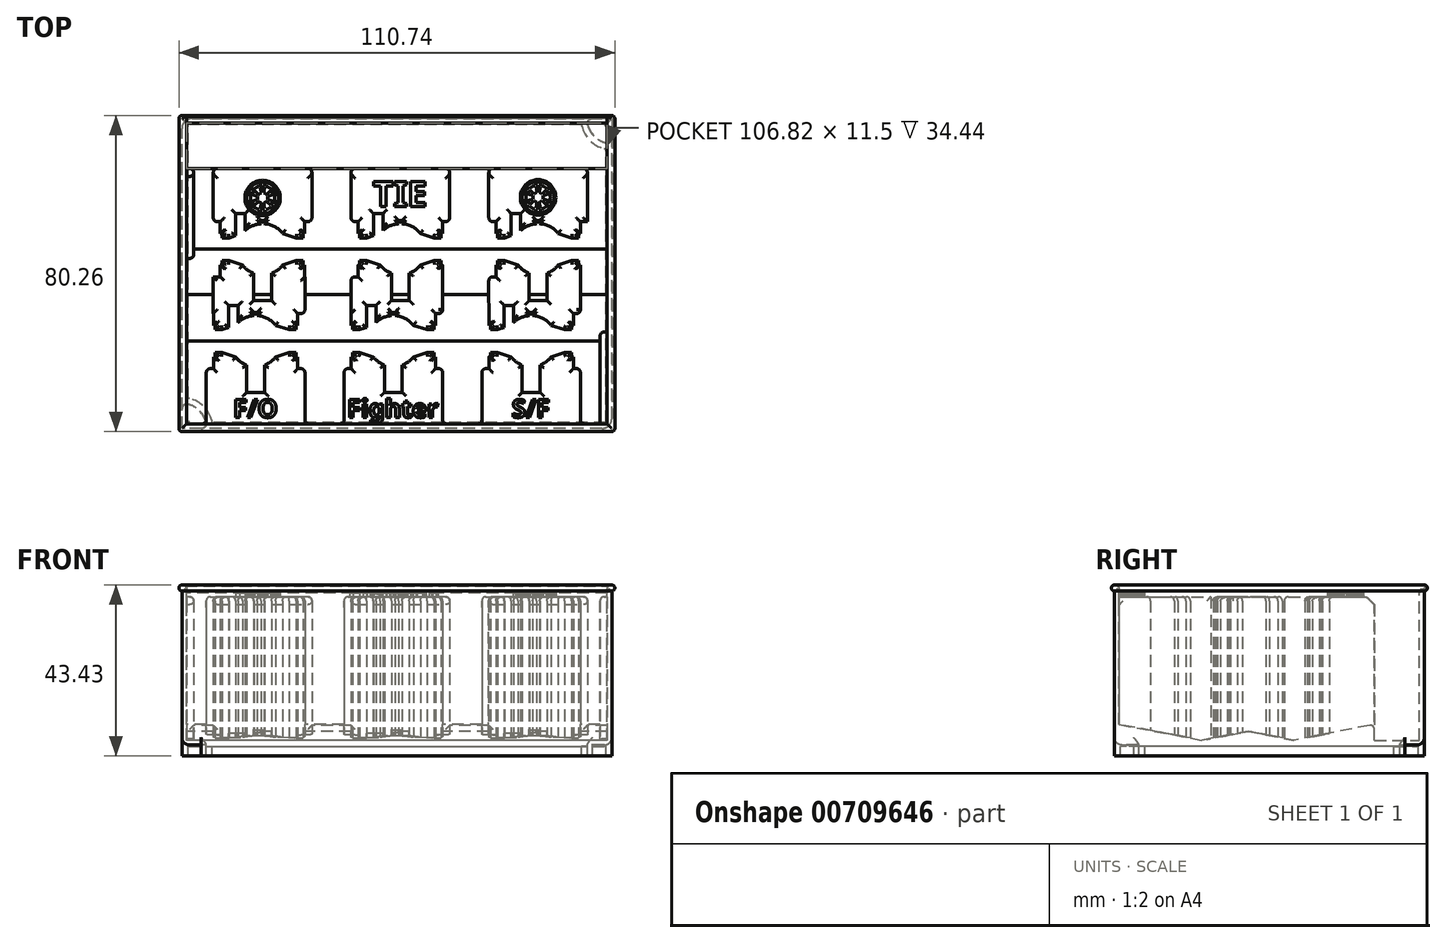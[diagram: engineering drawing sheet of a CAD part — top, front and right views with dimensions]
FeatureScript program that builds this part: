
annotation { "Feature Type Name" : "Feature", "Feature Type Description" : "" }
export const myFeature = defineFeature(function(context is Context, id is Id, definition is map)
    precondition{}
    {
        {
            var Q0;
            Q0=qCreatedBy(makeId("Front.planeOp"),FACE);
            var sketch = newSketch(context, id + "F0", { "sketchPlane" : qUnion([Q0])});
            skLineSegment(sketch, "E0.bottom", {"start": v(54.61, -20.32) * mm, "end": v(-54.61, -20.32) * mm});
            skLineSegment(sketch, "E0.top", {"start": v(54.61, 20.32) * mm, "end": v(-54.61, 20.32) * mm});
            skLineSegment(sketch, "E0.left", {"start": v(54.61, -20.32) * mm, "end": v(54.61, 20.32) * mm});
            skLineSegment(sketch, "E0.right", {"start": v(-54.61, -20.32) * mm, "end": v(-54.61, 20.32) * mm});
            skPoint(sketch, "E0.middle", {"position": v(0, 0) * mm});
            skSolve(sketch);
        }
        {
            var Q0;
            Q0=makeQuery(id+"F0.imprint","IMPRINT",FACE,{"disambiguationData":[TD([[makeQuery(id+"F0.imprint","IMPRINT",EDGE,{"derivedFrom":sQuery(id+"F0.wireOp",EDGE,"E0.bottom")}),-1.0]])]});
            extrude(context, id + "F1", {"entities" : qUnion([Q0]), "depth" : 78.74 * mm, "symmetric" : true});
        }
        {
            var Q0;
            Q0=makeQuery(id+"F1.opExtrude","SWEPT_FACE",FACE,{"disambiguationData":[OSD([sQuery(id+"F0.wireOp",EDGE,"E0.top")])]});
            shell(context, id + "F2", {"entities" : qUnion([Q0]), "thickness" : 1.2 * mm});
        }
        {
            var Q0;
            Q0=makeQuery(id+"F1.opExtrude","CAP_FACE",FACE,{"disambiguationData":[OSD([sQuery(id+"F0.wireOp",EDGE,"E0.bottom"),sQuery(id+"F0.wireOp",EDGE,"E0.top"),sQuery(id+"F0.wireOp",EDGE,"E0.left"),sQuery(id+"F0.wireOp",EDGE,"E0.right")])],"isStart":false});
            var sketch = newSketch(context, id + "F3", { "sketchPlane" : qUnion([Q0])});
            skArc(sketch, "E1", {"start": v(-54.61, 20.32) * mm, "mid": v(-55.37, 19.56) * mm, "end": v(-54.61, 18.8) * mm});
            skSolve(sketch);
        }
        {
            var Q0;
            {var subQ0=sQuery(id+"F3.wireOp",EDGE,"E1");Q0=makeQuery(id+"F3.imprint","IMPRINT",FACE,{"disambiguationData":[TD([[makeQuery(id+"F3.imprint","IMPRINT",EDGE,{"derivedFrom":subQ0}),1.0]])]});}
            var Q1;
            Q1=makeQuery(id+"F1.opExtrude","SWEPT_EDGE",EDGE,{"disambiguationData":[OSD([sQuery(id+"F0.wireOp",EDGE,"E0.top"),sQuery(id+"F0.wireOp",EDGE,"E0.right")])]});
            var Q2;
            Q2=makeQuery(id+"F1.opExtrude","CAP_EDGE",EDGE,{"disambiguationData":[OSD([sQuery(id+"F0.wireOp",EDGE,"E0.top")])],"isStart":true});
            var Q3;
            Q3=makeQuery(id+"F1.opExtrude","SWEPT_EDGE",EDGE,{"disambiguationData":[OSD([sQuery(id+"F0.wireOp",EDGE,"E0.top"),sQuery(id+"F0.wireOp",EDGE,"E0.left")])]});
            var Q4;
            Q4=makeQuery(id+"F1.opExtrude","CAP_EDGE",EDGE,{"disambiguationData":[OSD([sQuery(id+"F0.wireOp",EDGE,"E0.top")])],"isStart":false});
            sweep(context, id + "F4", {"operationType" : NewBodyOperationType.ADD, "profiles" : qUnion([Q0]), "path" : qUnion([Q1, Q2, Q3, Q4])});
        }
        {
            var Q0;
            Q0=makeQuery(id+"F1.opExtrude","SWEPT_FACE",FACE,{"disambiguationData":[OSD([sQuery(id+"F0.wireOp",EDGE,"E0.bottom")])]});
            var sketch = newSketch(context, id + "F5", { "sketchPlane" : qUnion([Q0])});
            skLineSegment(sketch, "E2.bottom", {"start": v(54.61, 39.37) * mm, "end": v(49.7, 39.37) * mm});
            skLineSegment(sketch, "E2.left", {"start": v(54.61, 39.37) * mm, "end": v(54.61, 34.45) * mm});
            skPoint(sketch, "E3.newPointA", {"position": v(48.26, 19.05) * mm});
            skArc(sketch, "E4", {"start": v(48.46, 37.78) * mm, "mid": v(50.12, 34.88) * mm, "end": v(53.02, 33.22) * mm});
            skPoint(sketch, "E5.visualSharp", {"position": v(48.26, 39.37) * mm});
            skArc(sketch, "E5.filletArc", {"start": v(49.7, 39.37) * mm, "mid": v(48.69, 38.88) * mm, "end": v(48.46, 37.78) * mm});
            skPoint(sketch, "E6.visualSharp", {"position": v(54.61, 33.02) * mm});
            skArc(sketch, "E6.filletArc", {"start": v(53.02, 33.22) * mm, "mid": v(54.12, 33.45) * mm, "end": v(54.6, 34.45) * mm});
            skArc(sketch, "E7.MirrorCS", {"start": v(-49.7, 39.37) * mm, "mid": v(-48.69, 38.88) * mm, "end": v(-48.46, 37.78) * mm});
            skArc(sketch, "E8.MirrorCS", {"start": v(-48.46, 37.78) * mm, "mid": v(-50.12, 34.88) * mm, "end": v(-53.02, 33.22) * mm});
            skArc(sketch, "E9.MirrorCS", {"start": v(-53.02, 33.22) * mm, "mid": v(-54.12, 33.45) * mm, "end": v(-54.6, 34.45) * mm});
            skLineSegment(sketch, "E10.MirrorCS", {"start": v(-54.61, 39.37) * mm, "end": v(-54.61, 34.45) * mm});
            skLineSegment(sketch, "E11.MirrorCS", {"start": v(-54.61, 39.37) * mm, "end": v(-49.7, 39.37) * mm});
            skArc(sketch, "E12.MirrorCS", {"start": v(-48.46, -37.78) * mm, "mid": v(-50.12, -34.88) * mm, "end": v(-53.02, -33.22) * mm});
            skArc(sketch, "E13.MirrorCS", {"start": v(-49.7, -39.37) * mm, "mid": v(-48.69, -38.88) * mm, "end": v(-48.46, -37.78) * mm});
            skLineSegment(sketch, "E14.MirrorCS", {"start": v(-54.6, -39.37) * mm, "end": v(-49.7, -39.37) * mm});
            skLineSegment(sketch, "E15.MirrorCS", {"start": v(-54.6, -39.37) * mm, "end": v(-54.6, -34.45) * mm});
            skArc(sketch, "E16.MirrorCS", {"start": v(-53.02, -33.22) * mm, "mid": v(-54.12, -33.45) * mm, "end": v(-54.6, -34.45) * mm});
            skArc(sketch, "E17.MirrorCS", {"start": v(49.7, -39.37) * mm, "mid": v(48.69, -38.88) * mm, "end": v(48.46, -37.78) * mm});
            skArc(sketch, "E18.MirrorCS", {"start": v(48.46, -37.78) * mm, "mid": v(50.12, -34.88) * mm, "end": v(53.02, -33.22) * mm});
            skArc(sketch, "E19.MirrorCS", {"start": v(53.02, -33.22) * mm, "mid": v(54.12, -33.45) * mm, "end": v(54.6, -34.45) * mm});
            skLineSegment(sketch, "E20.MirrorCS", {"start": v(54.6, -39.37) * mm, "end": v(54.6, -34.45) * mm});
            skLineSegment(sketch, "E21.MirrorCS", {"start": v(54.6, -39.37) * mm, "end": v(49.7, -39.37) * mm});
            skSolve(sketch);
        }
        {
            var Q0;
            Q0=makeQuery(id+"F5.imprint","IMPRINT",FACE,{"disambiguationData":[TD([[makeQuery(id+"F5.imprint","IMPRINT",EDGE,{"derivedFrom":sQuery(id+"F5.wireOp",EDGE,"E2.bottom")}),1.0]])]});
            var Q1;
            Q1=makeQuery(id+"F5.imprint","IMPRINT",FACE,{"disambiguationData":[TD([[makeQuery(id+"F5.imprint","IMPRINT",EDGE,{"derivedFrom":sQuery(id+"F5.wireOp",EDGE,"E8.MirrorCS")}),-1.0]])]});
            var Q2;
            Q2=makeQuery(id+"F5.imprint","IMPRINT",FACE,{"disambiguationData":[TD([[makeQuery(id+"F5.imprint","IMPRINT",EDGE,{"derivedFrom":sQuery(id+"F5.wireOp",EDGE,"E12.MirrorCS")}),1.0]])]});
            var Q3;
            Q3=makeQuery(id+"F5.imprint","IMPRINT",FACE,{"disambiguationData":[TD([[makeQuery(id+"F5.imprint","IMPRINT",EDGE,{"derivedFrom":sQuery(id+"F5.wireOp",EDGE,"E17.MirrorCS")}),-1.0]])]});
            extrude(context, id + "F6", {"entities" : qUnion([Q0, Q1, Q2, Q3]), "operationType" : NewBodyOperationType.ADD, "depth" : 2.8 * mm});
        }
        {
            var Q0;
            Q0=makeQuery(id+"F6.opExtrude","CAP_FACE",FACE,{"disambiguationData":[OSD([sQuery(id+"F5.wireOp",EDGE,"E2.bottom"),sQuery(id+"F5.wireOp",EDGE,"E2.left"),sQuery(id+"F5.wireOp",EDGE,"E4"),sQuery(id+"F5.wireOp",EDGE,"E5.filletArc"),sQuery(id+"F5.wireOp",EDGE,"E6.filletArc")])],"isStart":false});
            var Q1;
            Q1=makeQuery(id+"F6.opExtrude","CAP_FACE",FACE,{"disambiguationData":[OSD([sQuery(id+"F5.wireOp",EDGE,"E8.MirrorCS"),sQuery(id+"F5.wireOp",EDGE,"E9.MirrorCS"),sQuery(id+"F5.wireOp",EDGE,"E10.MirrorCS"),sQuery(id+"F5.wireOp",EDGE,"E7.MirrorCS"),sQuery(id+"F5.wireOp",EDGE,"E11.MirrorCS")])],"isStart":false});
            var Q2;
            Q2=makeQuery(id+"F6.opExtrude","CAP_FACE",FACE,{"disambiguationData":[OSD([sQuery(id+"F5.wireOp",EDGE,"E12.MirrorCS"),sQuery(id+"F5.wireOp",EDGE,"E13.MirrorCS"),sQuery(id+"F5.wireOp",EDGE,"E14.MirrorCS"),sQuery(id+"F5.wireOp",EDGE,"E15.MirrorCS"),sQuery(id+"F5.wireOp",EDGE,"E16.MirrorCS")])],"isStart":false});
            var Q3;
            Q3=makeQuery(id+"F6.opExtrude","CAP_FACE",FACE,{"disambiguationData":[OSD([sQuery(id+"F5.wireOp",EDGE,"E17.MirrorCS"),sQuery(id+"F5.wireOp",EDGE,"E18.MirrorCS"),sQuery(id+"F5.wireOp",EDGE,"E19.MirrorCS"),sQuery(id+"F5.wireOp",EDGE,"E20.MirrorCS"),sQuery(id+"F5.wireOp",EDGE,"E21.MirrorCS")])],"isStart":false});
            shell(context, id + "F7", {"entities" : qUnion([Q0, Q1, Q2, Q3]), "thickness" : 1.52 * mm});
        }
        {
            var Q0;
            Q0=makeQuery(id+"F1.opExtrude","SWEPT_EDGE",EDGE,{"disambiguationData":[OSD([sQuery(id+"F0.wireOp",EDGE,"E0.bottom"),sQuery(id+"F0.wireOp",EDGE,"E0.right")])]});
            var Q1;
            Q1=makeQuery(id+"F1.opExtrude","CAP_EDGE",EDGE,{"disambiguationData":[OSD([sQuery(id+"F0.wireOp",EDGE,"E0.bottom")])],"isStart":false});
            var Q2;
            Q2=makeQuery(id+"F1.opExtrude","SWEPT_EDGE",EDGE,{"disambiguationData":[OSD([sQuery(id+"F0.wireOp",EDGE,"E0.bottom"),sQuery(id+"F0.wireOp",EDGE,"E0.left")])]});
            var Q3;
            Q3=makeQuery(id+"F1.opExtrude","CAP_EDGE",EDGE,{"disambiguationData":[OSD([sQuery(id+"F0.wireOp",EDGE,"E0.bottom")])],"isStart":true});
            fillet(context, id + "F8", {"entities" : qUnion([Q0, Q1, Q2, Q3]), "radius" : 1.9 * mm, "tangentPropagation" : true, "allowEdgeOverflow" : false});
        }
        {
            var Q0;
            Q0=makeQuery(id+"F4.opSweep","MID_CAP_EDGE",EDGE,{"disambiguationData":[OSD([sQuery(id+"F0.wireOp",EDGE,"E0.top"),sQuery(id+"F0.wireOp",EDGE,"E0.left"),sQuery(id+"F3.wireOp",EDGE,"E1")])],"capPos":3.0});
            var Q1;
            Q1=makeQuery(id+"F4.opSweep","MID_CAP_EDGE",EDGE,{"disambiguationData":[OSD([sQuery(id+"F0.wireOp",EDGE,"E0.top"),sQuery(id+"F0.wireOp",EDGE,"E0.left"),sQuery(id+"F3.wireOp",EDGE,"E1")])],"capPos":2.0});
            var Q2;
            Q2=makeQuery(id+"F4.opSweep","MID_CAP_EDGE",EDGE,{"disambiguationData":[OSD([sQuery(id+"F0.wireOp",EDGE,"E0.top"),sQuery(id+"F0.wireOp",EDGE,"E0.right"),sQuery(id+"F3.wireOp",EDGE,"E1")])],"capPos":1.0});
            var Q3;
            Q3=makeQuery(id+"F4.opSweep","CAP_EDGE",EDGE,{"disambiguationData":[OSD([sQuery(id+"F0.wireOp",EDGE,"E0.top"),sQuery(id+"F0.wireOp",EDGE,"E0.right"),sQuery(id+"F3.wireOp",EDGE,"E1")])],"isStart":true});
            fillet(context, id + "F9", {"entities" : qUnion([Q0, Q1, Q2, Q3]), "radius" : 0.76 * mm, "tangentPropagation" : true, "allowEdgeOverflow" : false});
        }
        {
            var Q0;
            Q0=makeQuery(id+"F6.boolean.opBoolean","MERGE",EDGE,{"derivedFrom":[makeQuery(id+"F1.opExtrude","CAP_EDGE",EDGE,{"disambiguationData":[OSD([sQuery(id+"F0.wireOp",EDGE,"E0.left")])],"isStart":false}),makeQuery(id+"F6.opExtrude","SWEPT_EDGE",EDGE,{"disambiguationData":[OSD([sQuery(id+"F5.wireOp",EDGE,"E2.bottom"),sQuery(id+"F5.wireOp",EDGE,"E2.left")])]})]});
            var Q1;
            Q1=makeQuery(id+"F6.boolean.opBoolean","MERGE",EDGE,{"derivedFrom":[makeQuery(id+"F1.opExtrude","CAP_EDGE",EDGE,{"disambiguationData":[OSD([sQuery(id+"F0.wireOp",EDGE,"E0.left")])],"isStart":true}),makeQuery(id+"F6.opExtrude","SWEPT_EDGE",EDGE,{"disambiguationData":[OSD([sQuery(id+"F5.wireOp",EDGE,"E20.MirrorCS"),sQuery(id+"F5.wireOp",EDGE,"E21.MirrorCS")])]})]});
            var Q2;
            Q2=makeQuery(id+"F6.boolean.opBoolean","MERGE",EDGE,{"derivedFrom":[makeQuery(id+"F1.opExtrude","CAP_EDGE",EDGE,{"disambiguationData":[OSD([sQuery(id+"F0.wireOp",EDGE,"E0.right")])],"isStart":false}),makeQuery(id+"F6.opExtrude","SWEPT_EDGE",EDGE,{"disambiguationData":[OSD([sQuery(id+"F5.wireOp",EDGE,"E10.MirrorCS"),sQuery(id+"F5.wireOp",EDGE,"E11.MirrorCS")])]})]});
            var Q3;
            Q3=makeQuery(id+"F6.boolean.opBoolean","MERGE",EDGE,{"derivedFrom":[makeQuery(id+"F1.opExtrude","CAP_EDGE",EDGE,{"disambiguationData":[OSD([sQuery(id+"F0.wireOp",EDGE,"E0.right")])],"isStart":true}),makeQuery(id+"F6.opExtrude","SWEPT_EDGE",EDGE,{"disambiguationData":[OSD([sQuery(id+"F5.wireOp",EDGE,"E14.MirrorCS"),sQuery(id+"F5.wireOp",EDGE,"E15.MirrorCS")])]})]});
            fillet(context, id + "F10", {"entities" : qUnion([Q0, Q1, Q2, Q3]), "radius" : 2.54 * mm, "tangentPropagation" : true, "allowEdgeOverflow" : false});
        }
        {
            var Q0;
            Q0=makeQuery(id+"F2.opShell","OFFSET_FACE",FACE,{"disambiguationData":[OSD([sQuery(id+"F0.wireOp",EDGE,"E0.bottom")])]});
            var sketch = newSketch(context, id + "F11", { "sketchPlane" : qUnion([Q0])});
            skPoint(sketch, "E22.0", {"position": v(-53.4, -38.17) * mm});
            skArc(sketch, "E23", {"start": v(-41, -21.17) * mm, "mid": v(-39.72, -22.42) * mm, "end": v(-38.14, -23.27) * mm});
            skLineSegment(sketch, "E24.bottom", {"start": v(-23.36, -0.83) * mm, "end": v(-23.36, -10.17) * mm});
            skLineSegment(sketch, "E25.left", {"start": v(-27.36, -14.27) * mm, "end": v(-25.56, -14.27) * mm});
            skLineSegment(sketch, "E26", {"start": v(-30.76, -13.17) * mm, "end": v(-27.36, -14.27) * mm});
            skLineSegment(sketch, "E27.MirrorCS", {"start": v(-30.76, -21.17) * mm, "end": v(-27.36, -20.07) * mm});
            skLineSegment(sketch, "E28.MirrorCS", {"start": v(-27.36, -20.07) * mm, "end": v(-25.56, -20.07) * mm});
            skLineSegment(sketch, "E29.MirrorCS", {"start": v(-23.34, -38.17) * mm, "end": v(-18.34, -38.17) * mm});
            skLineSegment(sketch, "E30.MirrorCS", {"start": v(-44.4, -20.07) * mm, "end": v(-46.2, -20.07) * mm});
            skLineSegment(sketch, "E31.MirrorCS", {"start": v(-48.4, -38.17) * mm, "end": v(-53.4, -38.17) * mm});
            skLineSegment(sketch, "E32.MirrorCS", {"start": v(-42.7, -13.72) * mm, "end": v(-44.4, -14.27) * mm});
            skLineSegment(sketch, "E33.MirrorCS", {"start": v(-41, -21.17) * mm, "end": v(-44.4, -20.07) * mm});
            skLineSegment(sketch, "E34.MirrorCS", {"start": v(-53.4, 3.83) * mm, "end": v(-53.4, -17.17) * mm});
            skLineSegment(sketch, "E35.MirrorCS", {"start": v(-51.64, 3.83) * mm, "end": v(-53.4, 3.83) * mm});
            skArc(sketch, "E36.MirrorC", {"start": v(-40.3, -12.4) * mm, "mid": v(-38.45, -11.2) * mm, "end": v(-36.29, -10.68) * mm});
            skLineSegment(sketch, "E37.MirrorCS", {"start": v(-53.4, -38.17) * mm, "end": v(-53.4, -17.17) * mm});
            skLineSegment(sketch, "E38", {"start": v(-42.7, -13.72) * mm, "end": v(-42.7, -8.1) * mm});
            skLineSegment(sketch, "E39", {"start": v(-40.3, -12.4) * mm, "end": v(-40.3, -8.1) * mm});
            skLineSegment(sketch, "E40", {"start": v(-40.3, -8.1) * mm, "end": v(-42.7, -8.1) * mm});
            skArc(sketch, "E41.trimOffspring", {"start": v(-30.76, -13.17) * mm, "mid": v(-32.86, -11.42) * mm, "end": v(-35.49, -10.68) * mm});
            skArc(sketch, "E42.trimOffspring", {"start": v(-30.76, -21.17) * mm, "mid": v(-32.05, -22.42) * mm, "end": v(-33.64, -23.27) * mm});
            skLineSegment(sketch, "E43", {"start": v(-25.16, -13.17) * mm, "end": v(-25.56, -13.17) * mm});
            skLineSegment(sketch, "E44", {"start": v(-25.56, -13.17) * mm, "end": v(-25.56, -14.27) * mm});
            skLineSegment(sketch, "E45.MirrorCS", {"start": v(-25.56, -21.17) * mm, "end": v(-25.56, -20.07) * mm});
            skLineSegment(sketch, "E46.MirrorCS", {"start": v(-46.2, -13.17) * mm, "end": v(-46.2, -14.27) * mm});
            skLineSegment(sketch, "E47.MirrorCS", {"start": v(-46.2, -21.17) * mm, "end": v(-46.2, -20.07) * mm});
            skLineSegment(sketch, "E48", {"start": v(-46.2, -14.27) * mm, "end": v(-44.4, -14.27) * mm});
            skLineSegment(sketch, "E49", {"start": v(-38.14, -30.17) * mm, "end": v(-33.64, -30.17) * mm});
            skLineSegment(sketch, "E50", {"start": v(-38.14, -30.17) * mm, "end": v(-38.14, -23.27) * mm});
            skLineSegment(sketch, "E51", {"start": v(-33.64, -30.17) * mm, "end": v(-33.64, -23.27) * mm});
            skArc(sketch, "E52.trimOffspring", {"start": v(-38.14, -23.27) * mm, "mid": v(-39.72, -22.42) * mm, "end": v(-41, -21.17) * mm});
            skLineSegment(sketch, "E53", {"start": v(-35.89, -9.87) * mm, "end": v(-35.49, -9.87) * mm});
            skLineSegment(sketch, "E54", {"start": v(-35.49, -9.87) * mm, "end": v(-35.49, -10.68) * mm});
            skLineSegment(sketch, "E55", {"start": v(-35.89, -9.87) * mm, "end": v(-36.29, -9.87) * mm});
            skLineSegment(sketch, "E56", {"start": v(-36.29, -9.87) * mm, "end": v(-36.29, -10.68) * mm});
            skArc(sketch, "E57.trimOffspring", {"start": v(-35.49, -10.68) * mm, "mid": v(-32.86, -11.42) * mm, "end": v(-30.76, -13.17) * mm});
            skArc(sketch, "E58.trimOffspring", {"start": v(-36.29, -10.68) * mm, "mid": v(-38.45, -11.2) * mm, "end": v(-40.3, -12.4) * mm});
            skLineSegment(sketch, "E59.MirrorCS", {"start": v(-25.16, -21.17) * mm, "end": v(-25.56, -21.17) * mm});
            skLineSegment(sketch, "E60.MirrorCS", {"start": v(-46.6, -21.17) * mm, "end": v(-46.2, -21.17) * mm});
            skLineSegment(sketch, "E61.MirrorCS", {"start": v(-46.6, -13.17) * mm, "end": v(-46.2, -13.17) * mm});
            skLineSegment(sketch, "E62", {"start": v(-23.36, -10.17) * mm, "end": v(-25.16, -10.17) * mm});
            skLineSegment(sketch, "E63", {"start": v(-25.16, -10.17) * mm, "end": v(-25.16, -13.17) * mm});
            skLineSegment(sketch, "E64.MirrorCS", {"start": v(-23.36, -38.17) * mm, "end": v(-23.36, -24.17) * mm});
            skLineSegment(sketch, "E65.MirrorCS", {"start": v(-25.16, -24.17) * mm, "end": v(-25.16, -21.17) * mm});
            skLineSegment(sketch, "E66.MirrorCS", {"start": v(-23.36, -24.17) * mm, "end": v(-25.16, -24.17) * mm});
            skLineSegment(sketch, "E67.MirrorCS", {"start": v(-48.4, -38.17) * mm, "end": v(-48.4, -24.17) * mm});
            skLineSegment(sketch, "E68.MirrorCS", {"start": v(-48.41, -24.17) * mm, "end": v(-46.61, -24.17) * mm});
            skLineSegment(sketch, "E69.MirrorCS", {"start": v(-46.6, -24.17) * mm, "end": v(-46.6, -21.17) * mm});
            skLineSegment(sketch, "E70.MirrorCS", {"start": v(-46.6, -10.17) * mm, "end": v(-46.6, -13.17) * mm});
            skLineSegment(sketch, "E71.MirrorCS", {"start": v(-46.64, -10.17) * mm, "end": v(-46.61, -10.17) * mm});
            skLineSegment(sketch, "E72", {"start": v(-18.34, -38.17) * mm, "end": v(-17.54, -38.17) * mm, "construction": true});
            skPoint(sketch, "E73.1.0.0", {"position": v(-18.4, -38.17) * mm});
            skLineSegment(sketch, "E73.1.0.1", {"start": v(-6, -21.17) * mm, "end": v(-9.4, -20.07) * mm});
            skLineSegment(sketch, "E73.1.0.2", {"start": v(-5.3, -12.4) * mm, "end": v(-5.3, -8.1) * mm});
            skLineSegment(sketch, "E73.1.0.3", {"start": v(4.24, -13.17) * mm, "end": v(7.64, -14.27) * mm});
            skPoint(sketch, "E73.1.0.5", {"position": v(-0.89, -17.17) * mm});
            skLineSegment(sketch, "E73.1.0.10", {"start": v(11.66, -38.17) * mm, "end": v(16.66, -38.17) * mm});
            skLineSegment(sketch, "E73.1.0.11", {"start": v(1.36, -30.17) * mm, "end": v(1.36, -23.27) * mm});
            skLineSegment(sketch, "E73.1.0.12", {"start": v(11.64, -38.17) * mm, "end": v(11.64, -24.17) * mm});
            skArc(sketch, "E73.1.0.13", {"start": v(4.24, -13.17) * mm, "mid": v(2.14, -11.42) * mm, "end": v(-0.49, -10.68) * mm});
            skLineSegment(sketch, "E73.1.0.14", {"start": v(-11.61, -10.17) * mm, "end": v(-11.61, -13.17) * mm});
            skLineSegment(sketch, "E73.1.0.15", {"start": v(-3.14, -30.17) * mm, "end": v(1.36, -30.17) * mm});
            skLineSegment(sketch, "E73.1.0.16", {"start": v(-3.14, -30.17) * mm, "end": v(-3.14, -23.27) * mm});
            skLineSegment(sketch, "E73.1.0.18", {"start": v(-13.4, -38.17) * mm, "end": v(-18.4, -38.17) * mm});
            skLineSegment(sketch, "E73.1.0.19", {"start": v(-7.7, -13.72) * mm, "end": v(-7.7, -8.1) * mm});
            skArc(sketch, "E73.1.0.20", {"start": v(-0.49, -10.68) * mm, "mid": v(2.14, -11.42) * mm, "end": v(4.24, -13.17) * mm});
            skArc(sketch, "E73.1.0.23", {"start": v(-1.29, -10.68) * mm, "mid": v(-3.45, -11.2) * mm, "end": v(-5.3, -12.4) * mm});
            skLineSegment(sketch, "E73.1.0.24", {"start": v(4.24, -21.17) * mm, "end": v(7.64, -20.07) * mm});
            skLineSegment(sketch, "E73.1.0.25", {"start": v(-13.4, -38.17) * mm, "end": v(-13.4, -24.17) * mm});
            skLineSegment(sketch, "E73.1.0.26", {"start": v(9.84, -10.17) * mm, "end": v(9.84, -13.17) * mm});
            skArc(sketch, "E73.1.0.27", {"start": v(-5.3, -12.4) * mm, "mid": v(-3.45, -11.2) * mm, "end": v(-1.29, -10.68) * mm});
            skLineSegment(sketch, "E73.1.0.28", {"start": v(-13.4, -38.17) * mm, "end": v(-18.4, -38.17) * mm});
            skLineSegment(sketch, "E73.1.0.29", {"start": v(-7.7, -13.72) * mm, "end": v(-9.4, -14.27) * mm});
            skLineSegment(sketch, "E73.1.0.30", {"start": v(-11.64, -10.17) * mm, "end": v(-11.61, -10.17) * mm});
            skLineSegment(sketch, "E73.1.0.31", {"start": v(9.84, -21.17) * mm, "end": v(9.44, -21.17) * mm});
            skLineSegment(sketch, "E73.1.0.32", {"start": v(7.64, -20.07) * mm, "end": v(9.44, -20.07) * mm});
            skLineSegment(sketch, "E73.1.0.33", {"start": v(9.44, -21.17) * mm, "end": v(9.44, -20.07) * mm});
            skLineSegment(sketch, "E73.1.0.34", {"start": v(-11.6, -13.17) * mm, "end": v(-11.2, -13.17) * mm});
            skLineSegment(sketch, "E73.1.0.35", {"start": v(11.64, -24.17) * mm, "end": v(9.84, -24.17) * mm});
            skLineSegment(sketch, "E73.1.0.36", {"start": v(-11.2, -14.27) * mm, "end": v(-9.4, -14.27) * mm});
            skLineSegment(sketch, "E73.1.0.37", {"start": v(7.64, -14.27) * mm, "end": v(9.44, -14.27) * mm});
            skLineSegment(sketch, "E73.1.0.38", {"start": v(9.84, -24.17) * mm, "end": v(9.84, -21.17) * mm});
            skLineSegment(sketch, "E73.1.0.39", {"start": v(-13.4, -24.17) * mm, "end": v(-11.61, -24.17) * mm});
            skLineSegment(sketch, "E73.1.0.40", {"start": v(-11.6, -21.17) * mm, "end": v(-11.2, -21.17) * mm});
            skLineSegment(sketch, "E73.1.0.41", {"start": v(-9.4, -20.07) * mm, "end": v(-11.2, -20.07) * mm});
            skLineSegment(sketch, "E73.1.0.42", {"start": v(9.84, -13.17) * mm, "end": v(9.44, -13.17) * mm});
            skLineSegment(sketch, "E73.1.0.43", {"start": v(-11.61, -24.17) * mm, "end": v(-11.61, -21.17) * mm});
            skLineSegment(sketch, "E73.1.0.44", {"start": v(-5.3, -8.1) * mm, "end": v(-7.7, -8.1) * mm});
            skLineSegment(sketch, "E73.1.0.45", {"start": v(-11.2, -21.17) * mm, "end": v(-11.2, -20.07) * mm});
            skLineSegment(sketch, "E73.1.0.46", {"start": v(-11.2, -13.17) * mm, "end": v(-11.2, -14.27) * mm});
            skLineSegment(sketch, "E73.1.0.47", {"start": v(11.64, -10.17) * mm, "end": v(9.84, -10.17) * mm});
            skArc(sketch, "E73.1.0.48", {"start": v(4.24, -21.17) * mm, "mid": v(2.95, -22.42) * mm, "end": v(1.36, -23.27) * mm});
            skLineSegment(sketch, "E73.1.0.49", {"start": v(9.44, -13.17) * mm, "end": v(9.44, -14.27) * mm});
            skArc(sketch, "E73.1.0.50", {"start": v(-6, -21.17) * mm, "mid": v(-4.72, -22.42) * mm, "end": v(-3.14, -23.27) * mm});
            skLineSegment(sketch, "E73.1.0.51", {"start": v(16.66, -38.17) * mm, "end": v(17.46, -38.17) * mm, "construction": true});
            skArc(sketch, "E73.1.0.52", {"start": v(-3.14, -23.27) * mm, "mid": v(-4.72, -22.42) * mm, "end": v(-6, -21.17) * mm});
            skLineSegment(sketch, "E73.1.0.53", {"start": v(-0.89, -9.87) * mm, "end": v(-1.29, -9.87) * mm});
            skLineSegment(sketch, "E73.1.0.54", {"start": v(-0.49, -9.87) * mm, "end": v(-0.49, -10.68) * mm});
            skLineSegment(sketch, "E73.1.0.55", {"start": v(-1.29, -9.87) * mm, "end": v(-1.29, -10.68) * mm});
            skLineSegment(sketch, "E73.1.0.56", {"start": v(-0.89, -9.87) * mm, "end": v(-0.49, -9.87) * mm});
            skPoint(sketch, "E73.2.0.0", {"position": v(16.6, -38.17) * mm});
            skLineSegment(sketch, "E73.2.0.1", {"start": v(29, -21.17) * mm, "end": v(25.6, -20.07) * mm});
            skLineSegment(sketch, "E73.2.0.2", {"start": v(29.7, -12.4) * mm, "end": v(29.7, -8.1) * mm});
            skLineSegment(sketch, "E73.2.0.3", {"start": v(39.24, -13.17) * mm, "end": v(42.64, -14.27) * mm});
            skPoint(sketch, "E73.2.0.5", {"position": v(34.11, -17.17) * mm});
            skLineSegment(sketch, "E73.2.0.10", {"start": v(46.66, -38.17) * mm, "end": v(51.66, -38.17) * mm});
            skLineSegment(sketch, "E73.2.0.11", {"start": v(36.36, -30.17) * mm, "end": v(36.36, -23.27) * mm});
            skLineSegment(sketch, "E73.2.0.12", {"start": v(46.64, -38.17) * mm, "end": v(46.64, -24.17) * mm});
            skArc(sketch, "E73.2.0.13", {"start": v(39.24, -13.17) * mm, "mid": v(37.14, -11.42) * mm, "end": v(34.51, -10.68) * mm});
            skLineSegment(sketch, "E73.2.0.15", {"start": v(31.86, -30.17) * mm, "end": v(36.36, -30.17) * mm});
            skLineSegment(sketch, "E73.2.0.16", {"start": v(31.86, -30.17) * mm, "end": v(31.86, -23.27) * mm});
            skLineSegment(sketch, "E73.2.0.18", {"start": v(21.6, -38.17) * mm, "end": v(16.6, -38.17) * mm});
            skLineSegment(sketch, "E73.2.0.19", {"start": v(27.3, -13.72) * mm, "end": v(27.3, -8.1) * mm});
            skArc(sketch, "E73.2.0.20", {"start": v(34.51, -10.68) * mm, "mid": v(37.14, -11.42) * mm, "end": v(39.24, -13.17) * mm});
            skArc(sketch, "E73.2.0.23", {"start": v(33.71, -10.68) * mm, "mid": v(31.55, -11.2) * mm, "end": v(29.7, -12.4) * mm});
            skLineSegment(sketch, "E73.2.0.24", {"start": v(39.24, -21.17) * mm, "end": v(42.64, -20.07) * mm});
            skLineSegment(sketch, "E73.2.0.25", {"start": v(21.6, -38.17) * mm, "end": v(21.6, -24.17) * mm});
            skLineSegment(sketch, "E73.2.0.26", {"start": v(44.84, -10.17) * mm, "end": v(44.84, -13.17) * mm});
            skArc(sketch, "E73.2.0.27", {"start": v(29.7, -12.4) * mm, "mid": v(31.55, -11.2) * mm, "end": v(33.71, -10.68) * mm});
            skLineSegment(sketch, "E73.2.0.28", {"start": v(21.6, -38.17) * mm, "end": v(16.6, -38.17) * mm});
            skLineSegment(sketch, "E73.2.0.29", {"start": v(27.3, -13.72) * mm, "end": v(25.6, -14.27) * mm});
            skLineSegment(sketch, "E73.2.0.31", {"start": v(44.84, -21.17) * mm, "end": v(44.44, -21.17) * mm});
            skLineSegment(sketch, "E73.2.0.32", {"start": v(42.64, -20.07) * mm, "end": v(44.44, -20.07) * mm});
            skLineSegment(sketch, "E73.2.0.33", {"start": v(44.44, -21.17) * mm, "end": v(44.44, -20.07) * mm});
            skLineSegment(sketch, "E73.2.0.34", {"start": v(23.4, -13.17) * mm, "end": v(23.8, -13.17) * mm});
            skLineSegment(sketch, "E73.2.0.35", {"start": v(46.64, -24.17) * mm, "end": v(44.84, -24.17) * mm});
            skLineSegment(sketch, "E73.2.0.36", {"start": v(23.8, -14.27) * mm, "end": v(25.6, -14.27) * mm});
            skLineSegment(sketch, "E73.2.0.37", {"start": v(42.64, -14.27) * mm, "end": v(44.44, -14.27) * mm});
            skLineSegment(sketch, "E73.2.0.38", {"start": v(44.84, -24.17) * mm, "end": v(44.84, -21.17) * mm});
            skLineSegment(sketch, "E73.2.0.39", {"start": v(21.6, -24.17) * mm, "end": v(23.4, -24.17) * mm});
            skLineSegment(sketch, "E73.2.0.40", {"start": v(23.4, -21.17) * mm, "end": v(23.8, -21.17) * mm});
            skLineSegment(sketch, "E73.2.0.41", {"start": v(25.6, -20.07) * mm, "end": v(23.8, -20.07) * mm});
            skLineSegment(sketch, "E73.2.0.42", {"start": v(44.84, -13.17) * mm, "end": v(44.44, -13.17) * mm});
            skLineSegment(sketch, "E73.2.0.43", {"start": v(23.4, -24.17) * mm, "end": v(23.4, -21.17) * mm});
            skLineSegment(sketch, "E73.2.0.44", {"start": v(29.7, -8.1) * mm, "end": v(27.3, -8.1) * mm});
            skLineSegment(sketch, "E73.2.0.45", {"start": v(23.8, -21.17) * mm, "end": v(23.8, -20.07) * mm});
            skLineSegment(sketch, "E73.2.0.46", {"start": v(23.8, -13.17) * mm, "end": v(23.8, -14.27) * mm});
            skLineSegment(sketch, "E73.2.0.47", {"start": v(46.64, -10.17) * mm, "end": v(44.84, -10.17) * mm});
            skArc(sketch, "E73.2.0.48", {"start": v(39.24, -21.17) * mm, "mid": v(37.95, -22.42) * mm, "end": v(36.36, -23.27) * mm});
            skLineSegment(sketch, "E73.2.0.49", {"start": v(44.44, -13.17) * mm, "end": v(44.44, -14.27) * mm});
            skArc(sketch, "E73.2.0.50", {"start": v(29, -21.17) * mm, "mid": v(30.28, -22.42) * mm, "end": v(31.86, -23.27) * mm});
            skLineSegment(sketch, "E73.2.0.51", {"start": v(51.66, -38.17) * mm, "end": v(52.46, -38.17) * mm, "construction": true});
            skArc(sketch, "E73.2.0.52", {"start": v(31.86, -23.27) * mm, "mid": v(30.28, -22.42) * mm, "end": v(29, -21.17) * mm});
            skLineSegment(sketch, "E73.2.0.53", {"start": v(34.11, -9.87) * mm, "end": v(33.71, -9.87) * mm});
            skLineSegment(sketch, "E73.2.0.54", {"start": v(34.51, -9.87) * mm, "end": v(34.51, -10.68) * mm});
            skLineSegment(sketch, "E73.2.0.55", {"start": v(33.71, -9.87) * mm, "end": v(33.71, -10.68) * mm});
            skLineSegment(sketch, "E73.2.0.56", {"start": v(34.11, -9.87) * mm, "end": v(34.51, -9.87) * mm});
            skLineSegment(sketch, "E73.direction1", {"start": v(-53.41, -38.17) * mm, "end": v(-18.4, -38.17) * mm, "construction": true});
            skPoint(sketch, "E74.0", {"position": v(-51.64, -14.83) * mm});
            skArc(sketch, "E75", {"start": v(-39.24, 2.17) * mm, "mid": v(-37.95, 0.92) * mm, "end": v(-36.36, 0.07) * mm});
            skLineSegment(sketch, "E76.bottom", {"start": v(-21.59, 27.17) * mm, "end": v(-21.59, 13.17) * mm});
            skLineSegment(sketch, "E77.left", {"start": v(-25.59, 9.07) * mm, "end": v(-23.79, 9.07) * mm});
            skLineSegment(sketch, "E78", {"start": v(-28.99, 10.17) * mm, "end": v(-25.59, 9.07) * mm});
            skLineSegment(sketch, "E79.MirrorCS", {"start": v(-28.99, 2.17) * mm, "end": v(-25.59, 3.27) * mm});
            skLineSegment(sketch, "E80.MirrorCS", {"start": v(-25.59, 3.27) * mm, "end": v(-23.79, 3.27) * mm});
            skLineSegment(sketch, "E81.MirrorCS", {"start": v(-42.64, 3.27) * mm, "end": v(-44.44, 3.27) * mm});
            skLineSegment(sketch, "E82.MirrorCS", {"start": v(-40.94, 9.62) * mm, "end": v(-42.64, 9.07) * mm});
            skLineSegment(sketch, "E83.MirrorCS", {"start": v(-39.24, 2.17) * mm, "end": v(-42.64, 3.27) * mm});
            skLineSegment(sketch, "E84.MirrorCS", {"start": v(-51.64, 27.17) * mm, "end": v(-51.64, 6.17) * mm});
            skArc(sketch, "E85.MirrorC", {"start": v(-38.54, 10.93) * mm, "mid": v(-36.67, 12.14) * mm, "end": v(-34.51, 12.66) * mm});
            skLineSegment(sketch, "E86.MirrorCS", {"start": v(-51.64, 3.83) * mm, "end": v(-51.64, 6.17) * mm});
            skLineSegment(sketch, "E87", {"start": v(-40.94, 9.62) * mm, "end": v(-40.94, 15.23) * mm});
            skLineSegment(sketch, "E88", {"start": v(-38.54, 10.93) * mm, "end": v(-38.54, 15.23) * mm});
            skLineSegment(sketch, "E89", {"start": v(-38.54, 15.23) * mm, "end": v(-40.94, 15.23) * mm});
            skArc(sketch, "E90.trimOffspring", {"start": v(-28.99, 10.17) * mm, "mid": v(-31.08, 11.92) * mm, "end": v(-33.71, 12.66) * mm});
            skArc(sketch, "E91.trimOffspring", {"start": v(-28.99, 2.17) * mm, "mid": v(-30.28, 0.92) * mm, "end": v(-31.86, 0.07) * mm});
            skLineSegment(sketch, "E92", {"start": v(-23.39, 10.17) * mm, "end": v(-23.79, 10.17) * mm});
            skLineSegment(sketch, "E93", {"start": v(-23.79, 10.17) * mm, "end": v(-23.79, 9.07) * mm});
            skLineSegment(sketch, "E94.MirrorCS", {"start": v(-23.79, 2.17) * mm, "end": v(-23.79, 3.27) * mm});
            skLineSegment(sketch, "E95.MirrorCS", {"start": v(-44.44, 10.17) * mm, "end": v(-44.44, 9.07) * mm});
            skLineSegment(sketch, "E96.MirrorCS", {"start": v(-44.44, 2.17) * mm, "end": v(-44.44, 3.27) * mm});
            skLineSegment(sketch, "E97", {"start": v(-44.44, 9.07) * mm, "end": v(-42.64, 9.07) * mm});
            skLineSegment(sketch, "E98", {"start": v(-36.36, -6.83) * mm, "end": v(-31.86, -6.83) * mm});
            skLineSegment(sketch, "E99", {"start": v(-36.36, -6.83) * mm, "end": v(-36.36, 0.07) * mm});
            skLineSegment(sketch, "E100", {"start": v(-31.86, -6.83) * mm, "end": v(-31.86, 0.07) * mm});
            skArc(sketch, "E101.trimOffspring", {"start": v(-36.36, 0.07) * mm, "mid": v(-37.95, 0.92) * mm, "end": v(-39.24, 2.17) * mm});
            skLineSegment(sketch, "E102", {"start": v(-34.11, 13.47) * mm, "end": v(-33.71, 13.47) * mm});
            skLineSegment(sketch, "E103", {"start": v(-33.71, 13.47) * mm, "end": v(-33.71, 12.66) * mm});
            skLineSegment(sketch, "E104", {"start": v(-34.11, 13.47) * mm, "end": v(-34.51, 13.47) * mm});
            skLineSegment(sketch, "E105", {"start": v(-34.51, 13.47) * mm, "end": v(-34.51, 12.66) * mm});
            skArc(sketch, "E106.trimOffspring", {"start": v(-33.71, 12.66) * mm, "mid": v(-31.08, 11.92) * mm, "end": v(-28.99, 10.17) * mm});
            skArc(sketch, "E107.trimOffspring", {"start": v(-34.51, 12.66) * mm, "mid": v(-36.67, 12.14) * mm, "end": v(-38.54, 10.93) * mm});
            skLineSegment(sketch, "E108.MirrorCS", {"start": v(-23.39, 2.17) * mm, "end": v(-23.79, 2.17) * mm});
            skLineSegment(sketch, "E109.MirrorCS", {"start": v(-44.84, 2.17) * mm, "end": v(-44.44, 2.17) * mm});
            skLineSegment(sketch, "E110.MirrorCS", {"start": v(-44.84, 10.17) * mm, "end": v(-44.44, 10.17) * mm});
            skLineSegment(sketch, "E111", {"start": v(-21.59, 13.17) * mm, "end": v(-23.39, 13.17) * mm});
            skLineSegment(sketch, "E112", {"start": v(-23.39, 13.17) * mm, "end": v(-23.39, 10.17) * mm});
            skLineSegment(sketch, "E113.MirrorCS", {"start": v(-23.39, -0.83) * mm, "end": v(-23.39, 2.17) * mm});
            skLineSegment(sketch, "E114.MirrorCS", {"start": v(-23.36, -0.83) * mm, "end": v(-23.39, -0.83) * mm});
            skLineSegment(sketch, "E115.MirrorCS", {"start": v(-46.64, -10.17) * mm, "end": v(-46.64, -0.83) * mm});
            skLineSegment(sketch, "E116.MirrorCS", {"start": v(-46.64, -0.83) * mm, "end": v(-44.84, -0.83) * mm});
            skLineSegment(sketch, "E117.MirrorCS", {"start": v(-44.84, -0.83) * mm, "end": v(-44.84, 2.17) * mm});
            skLineSegment(sketch, "E118.MirrorCS", {"start": v(-44.84, 13.17) * mm, "end": v(-44.84, 10.17) * mm});
            skLineSegment(sketch, "E119.MirrorCS", {"start": v(-46.64, 27.17) * mm, "end": v(-46.64, 13.17) * mm});
            skLineSegment(sketch, "E120.MirrorCS", {"start": v(-46.64, 13.17) * mm, "end": v(-44.84, 13.17) * mm});
            skLineSegment(sketch, "E121.1.0.1", {"start": v(-4.24, 2.17) * mm, "end": v(-7.64, 3.27) * mm});
            skLineSegment(sketch, "E121.1.0.2", {"start": v(-3.54, 10.93) * mm, "end": v(-3.54, 15.23) * mm});
            skLineSegment(sketch, "E121.1.0.3", {"start": v(6.01, 10.17) * mm, "end": v(9.4, 9.07) * mm});
            skPoint(sketch, "E121.1.0.5", {"position": v(0.89, 6.17) * mm});
            skLineSegment(sketch, "E121.1.0.8", {"start": v(13.41, 27.17) * mm, "end": v(13.41, 13.17) * mm});
            skLineSegment(sketch, "E121.1.0.11", {"start": v(3.14, -6.83) * mm, "end": v(3.14, 0.07) * mm});
            skArc(sketch, "E121.1.0.13", {"start": v(6.01, 10.17) * mm, "mid": v(3.92, 11.92) * mm, "end": v(1.29, 12.66) * mm});
            skLineSegment(sketch, "E121.1.0.14", {"start": v(-9.84, 13.17) * mm, "end": v(-9.84, 10.17) * mm});
            skLineSegment(sketch, "E121.1.0.15", {"start": v(-1.36, -6.83) * mm, "end": v(3.14, -6.83) * mm});
            skLineSegment(sketch, "E121.1.0.16", {"start": v(-1.36, -6.83) * mm, "end": v(-1.36, 0.07) * mm});
            skLineSegment(sketch, "E121.1.0.19", {"start": v(-5.94, 9.62) * mm, "end": v(-5.94, 15.23) * mm});
            skArc(sketch, "E121.1.0.20", {"start": v(1.29, 12.66) * mm, "mid": v(3.92, 11.92) * mm, "end": v(6.01, 10.17) * mm});
            skLineSegment(sketch, "E121.1.0.22", {"start": v(-11.64, 27.17) * mm, "end": v(-11.64, 13.17) * mm});
            skArc(sketch, "E121.1.0.23", {"start": v(0.49, 12.66) * mm, "mid": v(-1.67, 12.14) * mm, "end": v(-3.54, 10.93) * mm});
            skLineSegment(sketch, "E121.1.0.24", {"start": v(6.01, 2.17) * mm, "end": v(9.41, 3.27) * mm});
            skLineSegment(sketch, "E121.1.0.25", {"start": v(-11.64, -10.17) * mm, "end": v(-11.64, -0.83) * mm});
            skLineSegment(sketch, "E121.1.0.26", {"start": v(11.61, 13.17) * mm, "end": v(11.61, 10.17) * mm});
            skArc(sketch, "E121.1.0.27", {"start": v(-3.54, 10.93) * mm, "mid": v(-1.67, 12.14) * mm, "end": v(0.49, 12.66) * mm});
            skLineSegment(sketch, "E121.1.0.29", {"start": v(-5.94, 9.62) * mm, "end": v(-7.64, 9.07) * mm});
            skLineSegment(sketch, "E121.1.0.30", {"start": v(-11.64, 13.17) * mm, "end": v(-9.84, 13.17) * mm});
            skLineSegment(sketch, "E121.1.0.31", {"start": v(11.61, 2.17) * mm, "end": v(11.21, 2.17) * mm});
            skLineSegment(sketch, "E121.1.0.32", {"start": v(9.41, 3.27) * mm, "end": v(11.21, 3.27) * mm});
            skLineSegment(sketch, "E121.1.0.33", {"start": v(11.21, 2.17) * mm, "end": v(11.21, 3.27) * mm});
            skLineSegment(sketch, "E121.1.0.34", {"start": v(-9.84, 10.17) * mm, "end": v(-9.44, 10.17) * mm});
            skLineSegment(sketch, "E121.1.0.36", {"start": v(-9.44, 9.07) * mm, "end": v(-7.64, 9.07) * mm});
            skLineSegment(sketch, "E121.1.0.37", {"start": v(9.41, 9.07) * mm, "end": v(11.21, 9.07) * mm});
            skLineSegment(sketch, "E121.1.0.38", {"start": v(11.61, -0.83) * mm, "end": v(11.61, 2.17) * mm});
            skLineSegment(sketch, "E121.1.0.39", {"start": v(-11.64, -0.83) * mm, "end": v(-9.84, -0.83) * mm});
            skLineSegment(sketch, "E121.1.0.40", {"start": v(-9.84, 2.17) * mm, "end": v(-9.44, 2.17) * mm});
            skLineSegment(sketch, "E121.1.0.41", {"start": v(-7.64, 3.27) * mm, "end": v(-9.44, 3.27) * mm});
            skLineSegment(sketch, "E121.1.0.42", {"start": v(11.61, 10.17) * mm, "end": v(11.21, 10.17) * mm});
            skLineSegment(sketch, "E121.1.0.43", {"start": v(-9.84, -0.83) * mm, "end": v(-9.84, 2.17) * mm});
            skLineSegment(sketch, "E121.1.0.44", {"start": v(-3.54, 15.23) * mm, "end": v(-5.94, 15.23) * mm});
            skLineSegment(sketch, "E121.1.0.45", {"start": v(-9.44, 2.17) * mm, "end": v(-9.44, 3.27) * mm});
            skLineSegment(sketch, "E121.1.0.46", {"start": v(-9.44, 10.17) * mm, "end": v(-9.44, 9.07) * mm});
            skLineSegment(sketch, "E121.1.0.47", {"start": v(13.41, 13.17) * mm, "end": v(11.61, 13.17) * mm});
            skArc(sketch, "E121.1.0.48", {"start": v(6.01, 2.17) * mm, "mid": v(4.72, 0.92) * mm, "end": v(3.14, 0.07) * mm});
            skLineSegment(sketch, "E121.1.0.49", {"start": v(11.21, 10.17) * mm, "end": v(11.21, 9.07) * mm});
            skArc(sketch, "E121.1.0.50", {"start": v(-4.24, 2.17) * mm, "mid": v(-2.95, 0.92) * mm, "end": v(-1.36, 0.07) * mm});
            skArc(sketch, "E121.1.0.52", {"start": v(-1.36, 0.07) * mm, "mid": v(-2.95, 0.92) * mm, "end": v(-4.24, 2.17) * mm});
            skLineSegment(sketch, "E121.1.0.53", {"start": v(0.89, 13.47) * mm, "end": v(0.49, 13.47) * mm});
            skLineSegment(sketch, "E121.1.0.54", {"start": v(1.29, 13.47) * mm, "end": v(1.29, 12.66) * mm});
            skLineSegment(sketch, "E121.1.0.55", {"start": v(0.49, 13.47) * mm, "end": v(0.49, 12.66) * mm});
            skLineSegment(sketch, "E121.1.0.56", {"start": v(0.89, 13.47) * mm, "end": v(1.29, 13.47) * mm});
            skLineSegment(sketch, "E121.2.0.1", {"start": v(30.76, 2.17) * mm, "end": v(27.36, 3.27) * mm});
            skLineSegment(sketch, "E121.2.0.2", {"start": v(31.46, 10.93) * mm, "end": v(31.46, 15.23) * mm});
            skLineSegment(sketch, "E121.2.0.3", {"start": v(41.01, 10.17) * mm, "end": v(44.4, 9.07) * mm});
            skLineSegment(sketch, "E121.2.0.4", {"start": v(53.44, -14.83) * mm, "end": v(53.44, 6.17) * mm});
            skPoint(sketch, "E121.2.0.5", {"position": v(35.89, 6.17) * mm});
            skLineSegment(sketch, "E121.2.0.8", {"start": v(48.41, 27.17) * mm, "end": v(48.41, 13.17) * mm});
            skLineSegment(sketch, "E121.2.0.9", {"start": v(53.41, 27.17) * mm, "end": v(53.41, 6.17) * mm});
            skLineSegment(sketch, "E121.2.0.11", {"start": v(38.14, -6.83) * mm, "end": v(38.14, 0.07) * mm});
            skArc(sketch, "E121.2.0.13", {"start": v(41.01, 10.17) * mm, "mid": v(38.92, 11.92) * mm, "end": v(36.29, 12.66) * mm});
            skLineSegment(sketch, "E121.2.0.14", {"start": v(25.16, 13.17) * mm, "end": v(25.16, 10.17) * mm});
            skLineSegment(sketch, "E121.2.0.15", {"start": v(33.64, -6.83) * mm, "end": v(38.14, -6.83) * mm});
            skLineSegment(sketch, "E121.2.0.16", {"start": v(33.64, -6.83) * mm, "end": v(33.64, 0.07) * mm});
            skLineSegment(sketch, "E121.2.0.19", {"start": v(29.06, 9.62) * mm, "end": v(29.06, 15.23) * mm});
            skArc(sketch, "E121.2.0.20", {"start": v(36.29, 12.66) * mm, "mid": v(38.92, 11.92) * mm, "end": v(41.01, 10.17) * mm});
            skLineSegment(sketch, "E121.2.0.22", {"start": v(23.36, 27.17) * mm, "end": v(23.36, 13.17) * mm});
            skArc(sketch, "E121.2.0.23", {"start": v(35.49, 12.66) * mm, "mid": v(33.33, 12.14) * mm, "end": v(31.46, 10.93) * mm});
            skLineSegment(sketch, "E121.2.0.24", {"start": v(41.01, 2.17) * mm, "end": v(44.41, 3.27) * mm});
            skLineSegment(sketch, "E121.2.0.26", {"start": v(46.61, 13.17) * mm, "end": v(46.61, 10.17) * mm});
            skArc(sketch, "E121.2.0.27", {"start": v(31.46, 10.93) * mm, "mid": v(33.33, 12.14) * mm, "end": v(35.49, 12.66) * mm});
            skLineSegment(sketch, "E121.2.0.29", {"start": v(29.06, 9.62) * mm, "end": v(27.36, 9.07) * mm});
            skLineSegment(sketch, "E121.2.0.30", {"start": v(23.36, 13.17) * mm, "end": v(25.16, 13.17) * mm});
            skLineSegment(sketch, "E121.2.0.31", {"start": v(46.6, 2.17) * mm, "end": v(46.21, 2.17) * mm});
            skLineSegment(sketch, "E121.2.0.32", {"start": v(44.41, 3.27) * mm, "end": v(46.21, 3.27) * mm});
            skLineSegment(sketch, "E121.2.0.33", {"start": v(46.21, 2.17) * mm, "end": v(46.21, 3.27) * mm});
            skLineSegment(sketch, "E121.2.0.34", {"start": v(25.16, 10.17) * mm, "end": v(25.56, 10.17) * mm});
            skLineSegment(sketch, "E121.2.0.36", {"start": v(25.56, 9.07) * mm, "end": v(27.36, 9.07) * mm});
            skLineSegment(sketch, "E121.2.0.37", {"start": v(44.41, 9.07) * mm, "end": v(46.21, 9.07) * mm});
            skLineSegment(sketch, "E121.2.0.38", {"start": v(46.61, -0.83) * mm, "end": v(46.61, 2.17) * mm});
            skLineSegment(sketch, "E121.2.0.39", {"start": v(23.36, -0.83) * mm, "end": v(25.16, -0.83) * mm});
            skLineSegment(sketch, "E121.2.0.40", {"start": v(25.16, 2.17) * mm, "end": v(25.56, 2.17) * mm});
            skLineSegment(sketch, "E121.2.0.41", {"start": v(27.36, 3.27) * mm, "end": v(25.56, 3.27) * mm});
            skLineSegment(sketch, "E121.2.0.42", {"start": v(46.6, 10.17) * mm, "end": v(46.21, 10.17) * mm});
            skLineSegment(sketch, "E121.2.0.43", {"start": v(25.16, -0.83) * mm, "end": v(25.16, 2.17) * mm});
            skLineSegment(sketch, "E121.2.0.44", {"start": v(31.46, 15.23) * mm, "end": v(29.06, 15.23) * mm});
            skLineSegment(sketch, "E121.2.0.45", {"start": v(25.56, 2.17) * mm, "end": v(25.56, 3.27) * mm});
            skLineSegment(sketch, "E121.2.0.46", {"start": v(25.56, 10.17) * mm, "end": v(25.56, 9.07) * mm});
            skLineSegment(sketch, "E121.2.0.47", {"start": v(48.41, 13.17) * mm, "end": v(46.61, 13.17) * mm});
            skArc(sketch, "E121.2.0.48", {"start": v(41.01, 2.17) * mm, "mid": v(39.72, 0.92) * mm, "end": v(38.14, 0.07) * mm});
            skLineSegment(sketch, "E121.2.0.49", {"start": v(46.21, 10.17) * mm, "end": v(46.21, 9.07) * mm});
            skArc(sketch, "E121.2.0.50", {"start": v(30.76, 2.17) * mm, "mid": v(32.05, 0.92) * mm, "end": v(33.64, 0.07) * mm});
            skArc(sketch, "E121.2.0.52", {"start": v(33.64, 0.07) * mm, "mid": v(32.05, 0.92) * mm, "end": v(30.76, 2.17) * mm});
            skLineSegment(sketch, "E121.2.0.53", {"start": v(35.89, 13.47) * mm, "end": v(35.49, 13.47) * mm});
            skLineSegment(sketch, "E121.2.0.54", {"start": v(36.29, 13.47) * mm, "end": v(36.29, 12.66) * mm});
            skLineSegment(sketch, "E121.2.0.55", {"start": v(35.49, 13.47) * mm, "end": v(35.49, 12.66) * mm});
            skLineSegment(sketch, "E121.2.0.56", {"start": v(35.89, 13.47) * mm, "end": v(36.29, 13.47) * mm});
            skLineSegment(sketch, "E121.direction1", {"start": v(-21.59, -14.83) * mm, "end": v(-21.56, -14.83) * mm, "construction": true});
            skLineSegment(sketch, "E122", {"start": v(-53.4, 38.17) * mm, "end": v(-53.4, 26.67) * mm});
            skLineSegment(sketch, "E123", {"start": v(53.41, 26.67) * mm, "end": v(53.41, 38.17) * mm});
            skLineSegment(sketch, "E124", {"start": v(53.41, 38.17) * mm, "end": v(-53.4, 38.17) * mm});
            skLineSegment(sketch, "E125", {"start": v(-53.4, 26.67) * mm, "end": v(-53.4, 25.47) * mm});
            skLineSegment(sketch, "E126", {"start": v(53.41, 25.47) * mm, "end": v(53.41, 26.67) * mm});
            skPoint(sketch, "E127.orphan", {"position": v(-11.64, 27.17) * mm});
            skLineSegment(sketch, "E128.trimOffspring", {"start": v(-11.64, 26.67) * mm, "end": v(13.41, 26.67) * mm});
            skLineSegment(sketch, "E129.trimOffspring", {"start": v(-46.64, 26.67) * mm, "end": v(-21.59, 26.67) * mm});
            skLineSegment(sketch, "E130.trimOffspring", {"start": v(23.36, 26.67) * mm, "end": v(48.41, 26.67) * mm});
            skPoint(sketch, "E131.orphan", {"position": v(23.36, 27.17) * mm});
            skPoint(sketch, "E132.orphan", {"position": v(-46.64, -14.83) * mm});
            skPoint(sketch, "E133.orphan", {"position": v(-11.64, -14.83) * mm});
            skPoint(sketch, "E134.orphan", {"position": v(48.44, -14.83) * mm});
            skLineSegment(sketch, "E135", {"start": v(23.36, -0.83) * mm, "end": v(23.4, -13.17) * mm});
            skLineSegment(sketch, "E136", {"start": v(46.61, -0.83) * mm, "end": v(46.64, -10.17) * mm});
            skLineSegment(sketch, "E137", {"start": v(11.61, -0.83) * mm, "end": v(11.64, -10.17) * mm});
            skLineSegment(sketch, "E138", {"start": v(-53.4, 26.67) * mm, "end": v(-51.64, 26.67) * mm});
            skLineSegment(sketch, "E139", {"start": v(53.44, -14.83) * mm, "end": v(53.4, -38.17) * mm});
            skLineSegment(sketch, "E140", {"start": v(53.4, -38.17) * mm, "end": v(51.66, -38.17) * mm});
            skLineSegment(sketch, "E141", {"start": v(51.64, -14.83) * mm, "end": v(51.66, -38.17) * mm});
            skLineSegment(sketch, "E142", {"start": v(51.64, -14.83) * mm, "end": v(53.44, -14.83) * mm});
            skSolve(sketch);
        }
        {
            var Q0;
            Q0=makeQuery(id+"F2.opShell","OFFSET_FACE",FACE,{"disambiguationData":[OSD([sQuery(id+"F0.wireOp",EDGE,"E0.right")])]});
            var sketch = newSketch(context, id + "F12", { "sketchPlane" : qUnion([Q0])});
            skLineSegment(sketch, "E143.0", {"start": v(-38.17, -19.12) * mm, "end": v(38.17, -19.12) * mm});
            skPoint(sketch, "E144.0", {"position": v(26.67, -19.12) * mm});
            skPoint(sketch, "E144.1", {"position": v(3.83, -19.12) * mm});
            skPoint(sketch, "E144.2", {"position": v(-0.83, -19.12) * mm});
            skLineSegment(sketch, "E145", {"start": v(-38.17, -19.12) * mm, "end": v(-38.17, -15.12) * mm});
            skPoint(sketch, "E146.0", {"position": v(-17.17, -19.12) * mm});
            skPoint(sketch, "E147.0", {"position": v(6.17, -19.12) * mm});
            skLineSegment(sketch, "E148", {"start": v(-38.17, -15.12) * mm, "end": v(-17.17, -19.12) * mm});
            skLineSegment(sketch, "E149", {"start": v(26.67, -19.12) * mm, "end": v(26.67, -15.12) * mm});
            skLineSegment(sketch, "E150", {"start": v(26.67, -15.12) * mm, "end": v(6.17, -19.12) * mm});
            skLineSegment(sketch, "E151.MirrorCS", {"start": v(-5.36, -16.87) * mm, "end": v(6.17, -19.12) * mm});
            skLineSegment(sketch, "E152.MirrorCS", {"start": v(-5.36, -16.87) * mm, "end": v(-17.17, -19.12) * mm});
            skSolve(sketch);
        }
        {
            var Q0;
            Q0 = qSketchRegion(id + "F12", true);
            var Q1;
            Q1=sQuery(id+"F11.wireOp",VERTEX,"E123.end");
            extrude(context, id + "F13", {"entities" : qUnion([Q0]), "operationType" : NewBodyOperationType.ADD, "endBound" : BoundingType.UP_TO_VERTEX, "depth" : 25 * mm, "endBoundEntityVertex" : qUnion([Q1]), "offsetDistance" : 25 * mm});
        }
        {
            var Q0;
            Q0=makeQuery(id+"F11.imprint","IMPRINT",FACE,{"disambiguationData":[TD([[makeQuery(id+"F11.imprint","IMPRINT",EDGE,{"derivedFrom":sQuery(id+"F11.wireOp",EDGE,"E24.bottom")}),-1.0]])]});
            var Q1;
            Q1=makeQuery(id+"F11.imprint","IMPRINT",FACE,{"disambiguationData":[TD([[makeQuery(id+"F11.imprint","IMPRINT",EDGE,{"derivedFrom":sQuery(id+"F11.wireOp",EDGE,"E73.1.0.2")}),-1.0]])]});
            var Q2;
            Q2=makeQuery(id+"F11.imprint","IMPRINT",FACE,{"disambiguationData":[TD([[makeQuery(id+"F11.imprint","IMPRINT",EDGE,{"derivedFrom":sQuery(id+"F11.wireOp",EDGE,"E73.2.0.2")}),-1.0]])]});
            var Q3;
            Q3=makeQuery(id+"F11.imprint","IMPRINT",FACE,{"disambiguationData":[TD([[makeQuery(id+"F11.imprint","IMPRINT",EDGE,{"derivedFrom":sQuery(id+"F11.wireOp",EDGE,"E77.left")}),1.0]])]});
            var Q4;
            Q4=makeQuery(id+"F11.imprint","IMPRINT",FACE,{"disambiguationData":[TD([[makeQuery(id+"F11.imprint","IMPRINT",EDGE,{"derivedFrom":sQuery(id+"F11.wireOp",EDGE,"E121.1.0.2")}),-1.0]])]});
            var Q5;
            Q5=makeQuery(id+"F11.imprint","IMPRINT",FACE,{"disambiguationData":[TD([[makeQuery(id+"F11.imprint","IMPRINT",EDGE,{"derivedFrom":sQuery(id+"F11.wireOp",EDGE,"E121.2.0.2")}),-1.0]])]});
            var Q6;
            {var subQ0=sQuery(id+"F11.wireOp",EDGE,"E139");Q6=makeQuery(id+"F11.imprint","IMPRINT",FACE,{"disambiguationData":[TD([[makeQuery(id+"F11.imprint","IMPRINT",EDGE,{"derivedFrom":subQ0}),-1.0]])]});}
            var Q7;
            Q7=makeQuery(id+"F11.imprint","IMPRINT",FACE,{"disambiguationData":[TD([[makeQuery(id+"F11.imprint","IMPRINT",EDGE,{"derivedFrom":sQuery(id+"F11.wireOp",EDGE,"E27.MirrorCS")}),-1.0]])]});
            var Q8;
            Q8=makeQuery(id+"F11.imprint","IMPRINT",FACE,{"disambiguationData":[TD([[makeQuery(id+"F11.imprint","IMPRINT",EDGE,{"derivedFrom":sQuery(id+"F11.wireOp",EDGE,"E73.1.0.1")}),1.0]])]});
            var Q9;
            Q9=makeQuery(id+"F11.imprint","IMPRINT",FACE,{"disambiguationData":[TD([[makeQuery(id+"F11.imprint","IMPRINT",EDGE,{"derivedFrom":sQuery(id+"F11.wireOp",EDGE,"E73.2.0.1")}),1.0]])]});
            var Q10;
            {var subQ4=sQuery(id+"F11.wireOp",EDGE,"E35.MirrorCS");Q10=makeQuery(id+"F11.imprint","IMPRINT",FACE,{"disambiguationData":[TD([[makeQuery(id+"F11.imprint","IMPRINT",EDGE,{"derivedFrom":subQ4}),-1.0]])]});}
            var Q11;
            {var subQ0=sQuery(id+"F11.wireOp",EDGE,"E140");Q11=makeQuery(id+"F11.imprint","IMPRINT",FACE,{"disambiguationData":[TD([[makeQuery(id+"F11.imprint","IMPRINT",EDGE,{"derivedFrom":subQ0}),-1.0]])]});}
            var Q12;
            {var subQ0=sQuery(id+"F0.wireOp",EDGE,"E0.right");var subQ1=sQuery(id+"F0.wireOp",EDGE,"E0.top");Q12=makeQuery(id+"F2.opShell","OFFSET_VERTEX",VERTEX,{"disambiguationData":[OSD([subQ1,subQ0]),TDD([makeQuery(id+"F1.opExtrude","CAP_VERTEX",VERTEX,{"disambiguationData":[OSD([subQ1,subQ0])],"isStart":true})])]});}
            extrude(context, id + "F14", {"entities" : qUnion([Q0, Q1, Q2, Q3, Q4, Q5, Q6, Q7, Q8, Q9, Q10, Q11]), "operationType" : NewBodyOperationType.ADD, "depth" : 36.44 * mm, "endBoundEntityVertex" : qUnion([Q12]), "offsetDistance" : 25 * mm});
        }
        {
            var Q0;
            Q0=makeQuery(id+"F14.opExtrude","CAP_EDGE",EDGE,{"disambiguationData":[OSD([sQuery(id+"F11.wireOp",EDGE,"E129.trimOffspring")])],"isStart":false});
            var Q1;
            Q1=makeQuery(id+"F14.opExtrude","CAP_EDGE",EDGE,{"disambiguationData":[OSD([sQuery(id+"F11.wireOp",EDGE,"E128.trimOffspring")])],"isStart":false});
            var Q2;
            Q2=makeQuery(id+"F14.opExtrude","CAP_EDGE",EDGE,{"disambiguationData":[OSD([sQuery(id+"F11.wireOp",EDGE,"E130.trimOffspring")])],"isStart":false});
            var Q3;
            Q3=makeQuery(id+"F14.opExtrude","CAP_EDGE",EDGE,{"disambiguationData":[OSD([sQuery(id+"F11.wireOp",EDGE,"E138")])],"isStart":false});
            var Q4;
            {var subQ0=sQuery(id+"F0.wireOp",EDGE,"E0.top");Q4=makeQuery(id+"F2.opShell","OFFSET_EDGE",EDGE,{"disambiguationData":[OSD([subQ0]),TDD([makeQuery(id+"F1.opExtrude","CAP_EDGE",EDGE,{"disambiguationData":[OSD([subQ0])],"isStart":true})])]});}
            chamfer(context, id + "F15", {"entities" : qUnion([Q0, Q1, Q2, Q3, Q4]), "width" : 2 * mm, "tangentPropagation" : true});
        }
        {
            var Q0;
            Q0=makeQuery(id+"F14.opExtrude","CAP_FACE",FACE,{"disambiguationData":[OSD([sQuery(id+"F11.wireOp",EDGE,"E24.bottom"),sQuery(id+"F11.wireOp",EDGE,"E25.left"),sQuery(id+"F11.wireOp",EDGE,"E26"),sQuery(id+"F11.wireOp",EDGE,"E32.MirrorCS"),sQuery(id+"F11.wireOp",EDGE,"E38"),sQuery(id+"F11.wireOp",EDGE,"E39"),sQuery(id+"F11.wireOp",EDGE,"E40"),sQuery(id+"F11.wireOp",EDGE,"E43"),sQuery(id+"F11.wireOp",EDGE,"E44"),sQuery(id+"F11.wireOp",EDGE,"E46.MirrorCS"),sQuery(id+"F11.wireOp",EDGE,"E48"),sQuery(id+"F11.wireOp",EDGE,"E53"),sQuery(id+"F11.wireOp",EDGE,"E54"),sQuery(id+"F11.wireOp",EDGE,"E55"),sQuery(id+"F11.wireOp",EDGE,"E56"),sQuery(id+"F11.wireOp",EDGE,"E57.trimOffspring"),sQuery(id+"F11.wireOp",EDGE,"E58.trimOffspring"),sQuery(id+"F11.wireOp",EDGE,"E61.MirrorCS"),sQuery(id+"F11.wireOp",EDGE,"E62"),sQuery(id+"F11.wireOp",EDGE,"E63"),sQuery(id+"F11.wireOp",EDGE,"E70.MirrorCS"),sQuery(id+"F11.wireOp",EDGE,"E71.MirrorCS"),sQuery(id+"F11.wireOp",EDGE,"E79.MirrorCS"),sQuery(id+"F11.wireOp",EDGE,"E80.MirrorCS"),sQuery(id+"F11.wireOp",EDGE,"E81.MirrorCS"),sQuery(id+"F11.wireOp",EDGE,"E83.MirrorCS"),sQuery(id+"F11.wireOp",EDGE,"E91.trimOffspring"),sQuery(id+"F11.wireOp",EDGE,"E94.MirrorCS"),sQuery(id+"F11.wireOp",EDGE,"E96.MirrorCS"),sQuery(id+"F11.wireOp",EDGE,"E98"),sQuery(id+"F11.wireOp",EDGE,"E99"),sQuery(id+"F11.wireOp",EDGE,"E100"),sQuery(id+"F11.wireOp",EDGE,"E101.trimOffspring"),sQuery(id+"F11.wireOp",EDGE,"E108.MirrorCS"),sQuery(id+"F11.wireOp",EDGE,"E109.MirrorCS"),sQuery(id+"F11.wireOp",EDGE,"E113.MirrorCS"),sQuery(id+"F11.wireOp",EDGE,"E114.MirrorCS"),sQuery(id+"F11.wireOp",EDGE,"E115.MirrorCS"),sQuery(id+"F11.wireOp",EDGE,"E116.MirrorCS"),sQuery(id+"F11.wireOp",EDGE,"E117.MirrorCS")])],"isStart":false});
            var Q1;
            Q1=makeQuery(id+"F14.opExtrude","CAP_FACE",FACE,{"disambiguationData":[OSD([sQuery(id+"F11.wireOp",EDGE,"E73.1.0.2"),sQuery(id+"F11.wireOp",EDGE,"E73.1.0.3"),sQuery(id+"F11.wireOp",EDGE,"E73.1.0.14"),sQuery(id+"F11.wireOp",EDGE,"E73.1.0.19"),sQuery(id+"F11.wireOp",EDGE,"E73.1.0.20"),sQuery(id+"F11.wireOp",EDGE,"E73.1.0.26"),sQuery(id+"F11.wireOp",EDGE,"E73.1.0.27"),sQuery(id+"F11.wireOp",EDGE,"E73.1.0.29"),sQuery(id+"F11.wireOp",EDGE,"E73.1.0.30"),sQuery(id+"F11.wireOp",EDGE,"E73.1.0.34"),sQuery(id+"F11.wireOp",EDGE,"E73.1.0.36"),sQuery(id+"F11.wireOp",EDGE,"E73.1.0.37"),sQuery(id+"F11.wireOp",EDGE,"E73.1.0.42"),sQuery(id+"F11.wireOp",EDGE,"E73.1.0.44"),sQuery(id+"F11.wireOp",EDGE,"E73.1.0.46"),sQuery(id+"F11.wireOp",EDGE,"E73.1.0.47"),sQuery(id+"F11.wireOp",EDGE,"E73.1.0.49"),sQuery(id+"F11.wireOp",EDGE,"E73.1.0.53"),sQuery(id+"F11.wireOp",EDGE,"E73.1.0.54"),sQuery(id+"F11.wireOp",EDGE,"E73.1.0.55"),sQuery(id+"F11.wireOp",EDGE,"E73.1.0.56"),sQuery(id+"F11.wireOp",EDGE,"E121.1.0.1"),sQuery(id+"F11.wireOp",EDGE,"E121.1.0.11"),sQuery(id+"F11.wireOp",EDGE,"E121.1.0.15"),sQuery(id+"F11.wireOp",EDGE,"E121.1.0.16"),sQuery(id+"F11.wireOp",EDGE,"E121.1.0.24"),sQuery(id+"F11.wireOp",EDGE,"E121.1.0.25"),sQuery(id+"F11.wireOp",EDGE,"E121.1.0.31"),sQuery(id+"F11.wireOp",EDGE,"E121.1.0.32"),sQuery(id+"F11.wireOp",EDGE,"E121.1.0.33"),sQuery(id+"F11.wireOp",EDGE,"E121.1.0.38"),sQuery(id+"F11.wireOp",EDGE,"E121.1.0.39"),sQuery(id+"F11.wireOp",EDGE,"E121.1.0.40"),sQuery(id+"F11.wireOp",EDGE,"E121.1.0.41"),sQuery(id+"F11.wireOp",EDGE,"E121.1.0.43"),sQuery(id+"F11.wireOp",EDGE,"E121.1.0.45"),sQuery(id+"F11.wireOp",EDGE,"E121.1.0.48"),sQuery(id+"F11.wireOp",EDGE,"E121.1.0.52"),sQuery(id+"F11.wireOp",EDGE,"E137")])],"isStart":false});
            var Q2;
            Q2=makeQuery(id+"F14.opExtrude","CAP_FACE",FACE,{"disambiguationData":[OSD([sQuery(id+"F11.wireOp",EDGE,"E73.2.0.2"),sQuery(id+"F11.wireOp",EDGE,"E73.2.0.3"),sQuery(id+"F11.wireOp",EDGE,"E73.2.0.19"),sQuery(id+"F11.wireOp",EDGE,"E73.2.0.20"),sQuery(id+"F11.wireOp",EDGE,"E73.2.0.26"),sQuery(id+"F11.wireOp",EDGE,"E73.2.0.27"),sQuery(id+"F11.wireOp",EDGE,"E73.2.0.29"),sQuery(id+"F11.wireOp",EDGE,"E73.2.0.34"),sQuery(id+"F11.wireOp",EDGE,"E73.2.0.36"),sQuery(id+"F11.wireOp",EDGE,"E73.2.0.37"),sQuery(id+"F11.wireOp",EDGE,"E73.2.0.42"),sQuery(id+"F11.wireOp",EDGE,"E73.2.0.44"),sQuery(id+"F11.wireOp",EDGE,"E73.2.0.46"),sQuery(id+"F11.wireOp",EDGE,"E73.2.0.47"),sQuery(id+"F11.wireOp",EDGE,"E73.2.0.49"),sQuery(id+"F11.wireOp",EDGE,"E73.2.0.53"),sQuery(id+"F11.wireOp",EDGE,"E73.2.0.54"),sQuery(id+"F11.wireOp",EDGE,"E73.2.0.55"),sQuery(id+"F11.wireOp",EDGE,"E73.2.0.56"),sQuery(id+"F11.wireOp",EDGE,"E121.2.0.1"),sQuery(id+"F11.wireOp",EDGE,"E121.2.0.11"),sQuery(id+"F11.wireOp",EDGE,"E121.2.0.15"),sQuery(id+"F11.wireOp",EDGE,"E121.2.0.16"),sQuery(id+"F11.wireOp",EDGE,"E121.2.0.24"),sQuery(id+"F11.wireOp",EDGE,"E121.2.0.31"),sQuery(id+"F11.wireOp",EDGE,"E121.2.0.32"),sQuery(id+"F11.wireOp",EDGE,"E121.2.0.33"),sQuery(id+"F11.wireOp",EDGE,"E121.2.0.38"),sQuery(id+"F11.wireOp",EDGE,"E121.2.0.39"),sQuery(id+"F11.wireOp",EDGE,"E121.2.0.40"),sQuery(id+"F11.wireOp",EDGE,"E121.2.0.41"),sQuery(id+"F11.wireOp",EDGE,"E121.2.0.43"),sQuery(id+"F11.wireOp",EDGE,"E121.2.0.45"),sQuery(id+"F11.wireOp",EDGE,"E121.2.0.48"),sQuery(id+"F11.wireOp",EDGE,"E121.2.0.52"),sQuery(id+"F11.wireOp",EDGE,"E135"),sQuery(id+"F11.wireOp",EDGE,"E136")])],"isStart":false});
            var Q3;
            Q3=makeQuery(id+"F14.opExtrude","CAP_FACE",FACE,{"disambiguationData":[OSD([sQuery(id+"F0.wireOp",EDGE,"E0.bottom"),sQuery(id+"F11.wireOp",EDGE,"E73.2.0.1"),sQuery(id+"F11.wireOp",EDGE,"E73.2.0.11"),sQuery(id+"F11.wireOp",EDGE,"E73.2.0.12"),sQuery(id+"F11.wireOp",EDGE,"E73.2.0.15"),sQuery(id+"F11.wireOp",EDGE,"E73.2.0.16"),sQuery(id+"F11.wireOp",EDGE,"E73.2.0.24"),sQuery(id+"F11.wireOp",EDGE,"E73.2.0.25"),sQuery(id+"F11.wireOp",EDGE,"E73.2.0.31"),sQuery(id+"F11.wireOp",EDGE,"E73.2.0.32"),sQuery(id+"F11.wireOp",EDGE,"E73.2.0.33"),sQuery(id+"F11.wireOp",EDGE,"E73.2.0.35"),sQuery(id+"F11.wireOp",EDGE,"E73.2.0.38"),sQuery(id+"F11.wireOp",EDGE,"E73.2.0.39"),sQuery(id+"F11.wireOp",EDGE,"E73.2.0.40"),sQuery(id+"F11.wireOp",EDGE,"E73.2.0.41"),sQuery(id+"F11.wireOp",EDGE,"E73.2.0.43"),sQuery(id+"F11.wireOp",EDGE,"E73.2.0.45"),sQuery(id+"F11.wireOp",EDGE,"E73.2.0.48"),sQuery(id+"F11.wireOp",EDGE,"E73.2.0.52")])],"isStart":false});
            var Q4;
            Q4=makeQuery(id+"F14.opExtrude","CAP_FACE",FACE,{"disambiguationData":[OSD([sQuery(id+"F0.wireOp",EDGE,"E0.bottom"),sQuery(id+"F11.wireOp",EDGE,"E73.1.0.1"),sQuery(id+"F11.wireOp",EDGE,"E73.1.0.11"),sQuery(id+"F11.wireOp",EDGE,"E73.1.0.12"),sQuery(id+"F11.wireOp",EDGE,"E73.1.0.15"),sQuery(id+"F11.wireOp",EDGE,"E73.1.0.16"),sQuery(id+"F11.wireOp",EDGE,"E73.1.0.24"),sQuery(id+"F11.wireOp",EDGE,"E73.1.0.25"),sQuery(id+"F11.wireOp",EDGE,"E73.1.0.31"),sQuery(id+"F11.wireOp",EDGE,"E73.1.0.32"),sQuery(id+"F11.wireOp",EDGE,"E73.1.0.33"),sQuery(id+"F11.wireOp",EDGE,"E73.1.0.35"),sQuery(id+"F11.wireOp",EDGE,"E73.1.0.38"),sQuery(id+"F11.wireOp",EDGE,"E73.1.0.39"),sQuery(id+"F11.wireOp",EDGE,"E73.1.0.40"),sQuery(id+"F11.wireOp",EDGE,"E73.1.0.41"),sQuery(id+"F11.wireOp",EDGE,"E73.1.0.43"),sQuery(id+"F11.wireOp",EDGE,"E73.1.0.45"),sQuery(id+"F11.wireOp",EDGE,"E73.1.0.48"),sQuery(id+"F11.wireOp",EDGE,"E73.1.0.52")])],"isStart":false});
            var Q5;
            Q5=makeQuery(id+"F14.opExtrude","CAP_FACE",FACE,{"disambiguationData":[OSD([sQuery(id+"F0.wireOp",EDGE,"E0.bottom"),sQuery(id+"F11.wireOp",EDGE,"E27.MirrorCS"),sQuery(id+"F11.wireOp",EDGE,"E28.MirrorCS"),sQuery(id+"F11.wireOp",EDGE,"E30.MirrorCS"),sQuery(id+"F11.wireOp",EDGE,"E33.MirrorCS"),sQuery(id+"F11.wireOp",EDGE,"E42.trimOffspring"),sQuery(id+"F11.wireOp",EDGE,"E45.MirrorCS"),sQuery(id+"F11.wireOp",EDGE,"E47.MirrorCS"),sQuery(id+"F11.wireOp",EDGE,"E49"),sQuery(id+"F11.wireOp",EDGE,"E50"),sQuery(id+"F11.wireOp",EDGE,"E51"),sQuery(id+"F11.wireOp",EDGE,"E52.trimOffspring"),sQuery(id+"F11.wireOp",EDGE,"E59.MirrorCS"),sQuery(id+"F11.wireOp",EDGE,"E60.MirrorCS"),sQuery(id+"F11.wireOp",EDGE,"E64.MirrorCS"),sQuery(id+"F11.wireOp",EDGE,"E65.MirrorCS"),sQuery(id+"F11.wireOp",EDGE,"E66.MirrorCS"),sQuery(id+"F11.wireOp",EDGE,"E67.MirrorCS"),sQuery(id+"F11.wireOp",EDGE,"E68.MirrorCS"),sQuery(id+"F11.wireOp",EDGE,"E69.MirrorCS")])],"isStart":false});
            var Q6;
            Q6=makeQuery(id+"F14.opExtrude","CAP_FACE",FACE,{"disambiguationData":[OSD([sQuery(id+"F11.wireOp",EDGE,"E76.bottom"),sQuery(id+"F11.wireOp",EDGE,"E77.left"),sQuery(id+"F11.wireOp",EDGE,"E78"),sQuery(id+"F11.wireOp",EDGE,"E82.MirrorCS"),sQuery(id+"F11.wireOp",EDGE,"E87"),sQuery(id+"F11.wireOp",EDGE,"E88"),sQuery(id+"F11.wireOp",EDGE,"E89"),sQuery(id+"F11.wireOp",EDGE,"E92"),sQuery(id+"F11.wireOp",EDGE,"E93"),sQuery(id+"F11.wireOp",EDGE,"E95.MirrorCS"),sQuery(id+"F11.wireOp",EDGE,"E97"),sQuery(id+"F11.wireOp",EDGE,"E102"),sQuery(id+"F11.wireOp",EDGE,"E103"),sQuery(id+"F11.wireOp",EDGE,"E104"),sQuery(id+"F11.wireOp",EDGE,"E105"),sQuery(id+"F11.wireOp",EDGE,"E106.trimOffspring"),sQuery(id+"F11.wireOp",EDGE,"E107.trimOffspring"),sQuery(id+"F11.wireOp",EDGE,"E110.MirrorCS"),sQuery(id+"F11.wireOp",EDGE,"E111"),sQuery(id+"F11.wireOp",EDGE,"E112"),sQuery(id+"F11.wireOp",EDGE,"E118.MirrorCS"),sQuery(id+"F11.wireOp",EDGE,"E119.MirrorCS"),sQuery(id+"F11.wireOp",EDGE,"E120.MirrorCS"),sQuery(id+"F11.wireOp",EDGE,"E129.trimOffspring")])],"isStart":false});
            var Q7;
            Q7=makeQuery(id+"F14.opExtrude","CAP_FACE",FACE,{"disambiguationData":[OSD([sQuery(id+"F11.wireOp",EDGE,"E121.1.0.2"),sQuery(id+"F11.wireOp",EDGE,"E121.1.0.3"),sQuery(id+"F11.wireOp",EDGE,"E121.1.0.8"),sQuery(id+"F11.wireOp",EDGE,"E121.1.0.14"),sQuery(id+"F11.wireOp",EDGE,"E121.1.0.19"),sQuery(id+"F11.wireOp",EDGE,"E121.1.0.20"),sQuery(id+"F11.wireOp",EDGE,"E121.1.0.22"),sQuery(id+"F11.wireOp",EDGE,"E121.1.0.26"),sQuery(id+"F11.wireOp",EDGE,"E121.1.0.27"),sQuery(id+"F11.wireOp",EDGE,"E121.1.0.29"),sQuery(id+"F11.wireOp",EDGE,"E121.1.0.30"),sQuery(id+"F11.wireOp",EDGE,"E121.1.0.34"),sQuery(id+"F11.wireOp",EDGE,"E121.1.0.36"),sQuery(id+"F11.wireOp",EDGE,"E121.1.0.37"),sQuery(id+"F11.wireOp",EDGE,"E121.1.0.42"),sQuery(id+"F11.wireOp",EDGE,"E121.1.0.44"),sQuery(id+"F11.wireOp",EDGE,"E121.1.0.46"),sQuery(id+"F11.wireOp",EDGE,"E121.1.0.47"),sQuery(id+"F11.wireOp",EDGE,"E121.1.0.49"),sQuery(id+"F11.wireOp",EDGE,"E121.1.0.53"),sQuery(id+"F11.wireOp",EDGE,"E121.1.0.54"),sQuery(id+"F11.wireOp",EDGE,"E121.1.0.55"),sQuery(id+"F11.wireOp",EDGE,"E121.1.0.56"),sQuery(id+"F11.wireOp",EDGE,"E128.trimOffspring")])],"isStart":false});
            var Q8;
            Q8=makeQuery(id+"F14.opExtrude","CAP_FACE",FACE,{"disambiguationData":[OSD([sQuery(id+"F11.wireOp",EDGE,"E121.2.0.2"),sQuery(id+"F11.wireOp",EDGE,"E121.2.0.3"),sQuery(id+"F11.wireOp",EDGE,"E121.2.0.8"),sQuery(id+"F11.wireOp",EDGE,"E121.2.0.14"),sQuery(id+"F11.wireOp",EDGE,"E121.2.0.19"),sQuery(id+"F11.wireOp",EDGE,"E121.2.0.20"),sQuery(id+"F11.wireOp",EDGE,"E121.2.0.22"),sQuery(id+"F11.wireOp",EDGE,"E121.2.0.26"),sQuery(id+"F11.wireOp",EDGE,"E121.2.0.27"),sQuery(id+"F11.wireOp",EDGE,"E121.2.0.29"),sQuery(id+"F11.wireOp",EDGE,"E121.2.0.30"),sQuery(id+"F11.wireOp",EDGE,"E121.2.0.34"),sQuery(id+"F11.wireOp",EDGE,"E121.2.0.36"),sQuery(id+"F11.wireOp",EDGE,"E121.2.0.37"),sQuery(id+"F11.wireOp",EDGE,"E121.2.0.42"),sQuery(id+"F11.wireOp",EDGE,"E121.2.0.44"),sQuery(id+"F11.wireOp",EDGE,"E121.2.0.46"),sQuery(id+"F11.wireOp",EDGE,"E121.2.0.47"),sQuery(id+"F11.wireOp",EDGE,"E121.2.0.49"),sQuery(id+"F11.wireOp",EDGE,"E121.2.0.53"),sQuery(id+"F11.wireOp",EDGE,"E121.2.0.54"),sQuery(id+"F11.wireOp",EDGE,"E121.2.0.55"),sQuery(id+"F11.wireOp",EDGE,"E121.2.0.56"),sQuery(id+"F11.wireOp",EDGE,"E130.trimOffspring")])],"isStart":false});
            var Q9;
            Q9=makeQuery(id+"F14.opExtrude","CAP_EDGE",EDGE,{"disambiguationData":[OSD([sQuery(id+"F11.wireOp",EDGE,"E35.MirrorCS")])],"isStart":false});
            var Q10;
            Q10=makeQuery(id+"F14.opExtrude","CAP_EDGE",EDGE,{"disambiguationData":[OSD([sQuery(id+"F0.wireOp",EDGE,"E0.bottom"),sQuery(id+"F0.wireOp",EDGE,"E0.right"),sQuery(id+"F11.wireOp",EDGE,"E125")])],"isStart":false});
            fillet(context, id + "F16", {"entities" : qUnion([Q0, Q1, Q2, Q3, Q4, Q5, Q6, Q7, Q8, Q9, Q10]), "radius" : 1 * mm, "tangentPropagation" : true, "allowEdgeOverflow" : false});
        }
        {
            var Q0;
            Q0=makeQuery(id+"F14.opExtrude","CAP_EDGE",EDGE,{"disambiguationData":[OSD([sQuery(id+"F11.wireOp",EDGE,"E84.MirrorCS"),sQuery(id+"F11.wireOp",EDGE,"E86.MirrorCS")])],"isStart":false});
            var Q1;
            Q1=makeQuery(id+"F14.opExtrude","SWEPT_EDGE",EDGE,{"disambiguationData":[OSD([sQuery(id+"F11.wireOp",EDGE,"E141"),sQuery(id+"F11.wireOp",EDGE,"E142")])]});
            var Q2;
            Q2=makeQuery(id+"F14.opExtrude","CAP_EDGE",EDGE,{"disambiguationData":[OSD([sQuery(id+"F11.wireOp",EDGE,"E141")])],"isStart":false});
            var Q3;
            Q3=makeQuery(id+"F14.opExtrude","SWEPT_EDGE",EDGE,{"disambiguationData":[OSD([sQuery(id+"F11.wireOp",EDGE,"E73.1.0.47"),sQuery(id+"F11.wireOp",EDGE,"E137")])]});
            var Q4;
            Q4=makeQuery(id+"F14.opExtrude","SWEPT_EDGE",EDGE,{"disambiguationData":[OSD([sQuery(id+"F11.wireOp",EDGE,"E24.bottom"),sQuery(id+"F11.wireOp",EDGE,"E62")])]});
            var Q5;
            Q5=makeQuery(id+"F14.opExtrude","SWEPT_EDGE",EDGE,{"disambiguationData":[OSD([sQuery(id+"F11.wireOp",EDGE,"E76.bottom"),sQuery(id+"F11.wireOp",EDGE,"E111")])]});
            var Q6;
            Q6=makeQuery(id+"F14.opExtrude","SWEPT_EDGE",EDGE,{"disambiguationData":[OSD([sQuery(id+"F11.wireOp",EDGE,"E121.1.0.8"),sQuery(id+"F11.wireOp",EDGE,"E121.1.0.47")])]});
            var Q7;
            Q7=makeQuery(id+"F14.opExtrude","SWEPT_EDGE",EDGE,{"disambiguationData":[OSD([sQuery(id+"F11.wireOp",EDGE,"E121.2.0.22"),sQuery(id+"F11.wireOp",EDGE,"E121.2.0.30")])]});
            var Q8;
            Q8=makeQuery(id+"F14.opExtrude","SWEPT_EDGE",EDGE,{"disambiguationData":[OSD([sQuery(id+"F11.wireOp",EDGE,"E121.1.0.22"),sQuery(id+"F11.wireOp",EDGE,"E121.1.0.30")])]});
            var Q9;
            Q9=makeQuery(id+"F14.opExtrude","SWEPT_EDGE",EDGE,{"disambiguationData":[OSD([sQuery(id+"F11.wireOp",EDGE,"E119.MirrorCS"),sQuery(id+"F11.wireOp",EDGE,"E120.MirrorCS")])]});
            var Q10;
            Q10=makeQuery(id+"F14.opExtrude","SWEPT_EDGE",EDGE,{"disambiguationData":[OSD([sQuery(id+"F11.wireOp",EDGE,"E121.1.0.25"),sQuery(id+"F11.wireOp",EDGE,"E121.1.0.39")])]});
            var Q11;
            Q11=makeQuery(id+"F14.opExtrude","SWEPT_EDGE",EDGE,{"disambiguationData":[OSD([sQuery(id+"F11.wireOp",EDGE,"E121.2.0.39"),sQuery(id+"F11.wireOp",EDGE,"E135")])]});
            var Q12;
            Q12=makeQuery(id+"F14.opExtrude","SWEPT_EDGE",EDGE,{"disambiguationData":[OSD([sQuery(id+"F11.wireOp",EDGE,"E73.1.0.25"),sQuery(id+"F11.wireOp",EDGE,"E73.1.0.39")])]});
            var Q13;
            Q13=makeQuery(id+"F14.opExtrude","SWEPT_EDGE",EDGE,{"disambiguationData":[OSD([sQuery(id+"F11.wireOp",EDGE,"E67.MirrorCS"),sQuery(id+"F11.wireOp",EDGE,"E68.MirrorCS")])]});
            var Q14;
            Q14=makeQuery(id+"F14.opExtrude","SWEPT_EDGE",EDGE,{"disambiguationData":[OSD([sQuery(id+"F11.wireOp",EDGE,"E73.2.0.25"),sQuery(id+"F11.wireOp",EDGE,"E73.2.0.39")])]});
            var Q15;
            Q15=makeQuery(id+"F14.opExtrude","SWEPT_EDGE",EDGE,{"disambiguationData":[OSD([sQuery(id+"F11.wireOp",EDGE,"E64.MirrorCS"),sQuery(id+"F11.wireOp",EDGE,"E66.MirrorCS")])]});
            var Q16;
            Q16=makeQuery(id+"F14.opExtrude","SWEPT_EDGE",EDGE,{"disambiguationData":[OSD([sQuery(id+"F11.wireOp",EDGE,"E73.1.0.12"),sQuery(id+"F11.wireOp",EDGE,"E73.1.0.35")])]});
            var Q17;
            Q17=makeQuery(id+"F14.opExtrude","SWEPT_EDGE",EDGE,{"disambiguationData":[OSD([sQuery(id+"F11.wireOp",EDGE,"E73.2.0.12"),sQuery(id+"F11.wireOp",EDGE,"E73.2.0.35")])]});
            var Q18;
            Q18=makeQuery(id+"F14.opExtrude","SWEPT_EDGE",EDGE,{"disambiguationData":[OSD([sQuery(id+"F11.wireOp",EDGE,"E73.2.0.47"),sQuery(id+"F11.wireOp",EDGE,"E136")])]});
            var Q19;
            Q19=makeQuery(id+"F2.opShell","OFFSET_EDGE",EDGE,{"disambiguationData":[OSD([sQuery(id+"F0.wireOp",EDGE,"E0.top"),sQuery(id+"F0.wireOp",EDGE,"E0.left")])]});
            var Q20;
            {var subQ0=sQuery(id+"F0.wireOp",EDGE,"E0.top");Q20=makeQuery(id+"F2.opShell","OFFSET_EDGE",EDGE,{"disambiguationData":[OSD([subQ0]),TDD([makeQuery(id+"F1.opExtrude","CAP_EDGE",EDGE,{"disambiguationData":[OSD([subQ0])],"isStart":false})])]});}
            var Q21;
            Q21=makeQuery(id+"F2.opShell","OFFSET_EDGE",EDGE,{"disambiguationData":[OSD([sQuery(id+"F0.wireOp",EDGE,"E0.top"),sQuery(id+"F0.wireOp",EDGE,"E0.right")])]});
            var Q22;
            {var subQ0=sQuery(id+"F12.wireOp",EDGE,"E150");var subQ1=sQuery(id+"F12.wireOp",EDGE,"E149");Q22=makeQuery(id+"F14.boolean.opBoolean","SPLIT",EDGE,{"disambiguationData":[TD([makeQuery(id+"F14.opExtrude","SWEPT_FACE",FACE,{"disambiguationData":[OSD([sQuery(id+"F11.wireOp",EDGE,"E119.MirrorCS")])]})])],"derivedFrom":makeQuery(id+"F13.opExtrude","SWEPT_EDGE",EDGE,{"disambiguationData":[OSD([subQ1,subQ0])]})});}
            var Q23;
            {var subQ0=sQuery(id+"F12.wireOp",EDGE,"E149");var subQ1=sQuery(id+"F12.wireOp",EDGE,"E150");Q23=makeQuery(id+"F14.boolean.opBoolean","SPLIT",EDGE,{"disambiguationData":[TD([makeQuery(id+"F14.opExtrude","SWEPT_FACE",FACE,{"disambiguationData":[OSD([sQuery(id+"F11.wireOp",EDGE,"E76.bottom")])]})])],"derivedFrom":makeQuery(id+"F13.opExtrude","SWEPT_EDGE",EDGE,{"disambiguationData":[OSD([subQ0,subQ1])]})});}
            var Q24;
            {var subQ0=sQuery(id+"F12.wireOp",EDGE,"E150");var subQ1=sQuery(id+"F12.wireOp",EDGE,"E149");Q24=makeQuery(id+"F14.boolean.opBoolean","SPLIT",EDGE,{"disambiguationData":[TD([makeQuery(id+"F14.opExtrude","SWEPT_FACE",FACE,{"disambiguationData":[OSD([sQuery(id+"F11.wireOp",EDGE,"E121.1.0.8")])]})])],"derivedFrom":makeQuery(id+"F13.opExtrude","SWEPT_EDGE",EDGE,{"disambiguationData":[OSD([subQ1,subQ0])]})});}
            var Q25;
            Q25=makeQuery(id+"F14.opExtrude","SWEPT_EDGE",EDGE,{"disambiguationData":[OSD([sQuery(id+"F11.wireOp",EDGE,"E84.MirrorCS"),sQuery(id+"F11.wireOp",EDGE,"E138")])]});
            var Q26;
            Q26=makeQuery(id+"F14.opExtrude","SWEPT_EDGE",EDGE,{"disambiguationData":[OSD([sQuery(id+"F11.wireOp",EDGE,"E76.bottom"),sQuery(id+"F11.wireOp",EDGE,"E129.trimOffspring")])]});
            var Q27;
            Q27=makeQuery(id+"F14.opExtrude","SWEPT_EDGE",EDGE,{"disambiguationData":[OSD([sQuery(id+"F11.wireOp",EDGE,"E121.1.0.8"),sQuery(id+"F11.wireOp",EDGE,"E128.trimOffspring")])]});
            var Q28;
            Q28=makeQuery(id+"F14.opExtrude","SWEPT_EDGE",EDGE,{"disambiguationData":[OSD([sQuery(id+"F11.wireOp",EDGE,"E121.2.0.8"),sQuery(id+"F11.wireOp",EDGE,"E130.trimOffspring")])]});
            var Q29;
            {var subQ0=sQuery(id+"F12.wireOp",EDGE,"E150");var subQ1=sQuery(id+"F12.wireOp",EDGE,"E149");Q29=makeQuery(id+"F14.boolean.opBoolean","SPLIT",EDGE,{"disambiguationData":[TD([makeQuery(id+"F2.opShell","OFFSET_FACE",FACE,{"disambiguationData":[OSD([sQuery(id+"F0.wireOp",EDGE,"E0.left")])]})])],"derivedFrom":makeQuery(id+"F13.opExtrude","SWEPT_EDGE",EDGE,{"disambiguationData":[OSD([subQ1,subQ0])]})});}
            var Q30;
            Q30=makeQuery(id+"F14.opExtrude","SWEPT_EDGE",EDGE,{"disambiguationData":[OSD([sQuery(id+"F11.wireOp",EDGE,"E121.2.0.22"),sQuery(id+"F11.wireOp",EDGE,"E130.trimOffspring")])]});
            var Q31;
            Q31=makeQuery(id+"F14.opExtrude","SWEPT_EDGE",EDGE,{"disambiguationData":[OSD([sQuery(id+"F11.wireOp",EDGE,"E121.1.0.22"),sQuery(id+"F11.wireOp",EDGE,"E128.trimOffspring")])]});
            var Q32;
            Q32=makeQuery(id+"F14.opExtrude","SWEPT_EDGE",EDGE,{"disambiguationData":[OSD([sQuery(id+"F11.wireOp",EDGE,"E119.MirrorCS"),sQuery(id+"F11.wireOp",EDGE,"E129.trimOffspring")])]});
            fillet(context, id + "F17", {"entities" : qUnion([Q0, Q1, Q2, Q3, Q4, Q5, Q6, Q7, Q8, Q9, Q10, Q11, Q12, Q13, Q14, Q15, Q16, Q17, Q18, Q19, Q20, Q21, Q22, Q23, Q24, Q25, Q26, Q27, Q28, Q29, Q30, Q31, Q32]), "radius" : 1 * mm, "tangentPropagation" : true, "allowEdgeOverflow" : false});
        }
        {
            var Q0;
            Q0=makeQuery(id+"F14.opExtrude","CAP_FACE",FACE,{"disambiguationData":[OSD([sQuery(id+"F11.wireOp",EDGE,"E76.bottom"),sQuery(id+"F11.wireOp",EDGE,"E77.left"),sQuery(id+"F11.wireOp",EDGE,"E78"),sQuery(id+"F11.wireOp",EDGE,"E82.MirrorCS"),sQuery(id+"F11.wireOp",EDGE,"E87"),sQuery(id+"F11.wireOp",EDGE,"E88"),sQuery(id+"F11.wireOp",EDGE,"E89"),sQuery(id+"F11.wireOp",EDGE,"E92"),sQuery(id+"F11.wireOp",EDGE,"E93"),sQuery(id+"F11.wireOp",EDGE,"E95.MirrorCS"),sQuery(id+"F11.wireOp",EDGE,"E97"),sQuery(id+"F11.wireOp",EDGE,"E102"),sQuery(id+"F11.wireOp",EDGE,"E103"),sQuery(id+"F11.wireOp",EDGE,"E104"),sQuery(id+"F11.wireOp",EDGE,"E105"),sQuery(id+"F11.wireOp",EDGE,"E106.trimOffspring"),sQuery(id+"F11.wireOp",EDGE,"E107.trimOffspring"),sQuery(id+"F11.wireOp",EDGE,"E110.MirrorCS"),sQuery(id+"F11.wireOp",EDGE,"E111"),sQuery(id+"F11.wireOp",EDGE,"E112"),sQuery(id+"F11.wireOp",EDGE,"E118.MirrorCS"),sQuery(id+"F11.wireOp",EDGE,"E119.MirrorCS"),sQuery(id+"F11.wireOp",EDGE,"E120.MirrorCS"),sQuery(id+"F11.wireOp",EDGE,"E129.trimOffspring")])],"isStart":false});
            var sketch = newSketch(context, id + "F18", { "sketchPlane" : qUnion([Q0])});
            skLineSegment(sketch, "E153", {"start": v(-34.11, 14.47) * mm, "end": v(-34.11, 24.26) * mm, "construction": true});
            skPoint(sketch, "E154", {"position": v(68.52, -28.47) * mm});
            skCircle(sketch, "E155", {"center": v(68.52, -28.47) * mm, "radius": 6.5 * mm});
            skArc(sketch, "E156", {"start": v(68.52, -34.97) * mm, "mid": v(75.02, -28.47) * mm, "end": v(68.52, -21.97) * mm});
            skArc(sketch, "E157", {"start": v(69.84, -23.54) * mm, "mid": v(69.34, -23.43) * mm, "end": v(68.82, -23.38) * mm});
            skArc(sketch, "E158", {"start": v(69.67, -32.75) * mm, "mid": v(70.74, -32.31) * mm, "end": v(71.66, -31.6) * mm});
            skPoint(sketch, "E159.startSnap0", {"position": v(68.52, -21.98) * mm});
            skLineSegment(sketch, "E160", {"start": v(68.82, -22.64) * mm, "end": v(68.82, -23.38) * mm});
            skArc(sketch, "E161.trimOffspring", {"start": v(73.45, -27.15) * mm, "mid": v(73.3, -26.66) * mm, "end": v(73.08, -26.18) * mm});
            skArc(sketch, "E162.trimOffspring", {"start": v(72.13, -32.07) * mm, "mid": v(72.48, -31.7) * mm, "end": v(72.78, -31.27) * mm});
            skLineSegment(sketch, "E163.trimOffspring", {"start": v(68.82, -23.38) * mm, "end": v(68.82, -22.64) * mm});
            skLineSegment(sketch, "E164.trimOffspring", {"start": v(72.78, -25.66) * mm, "end": v(73.41, -25.3) * mm});
            skLineSegment(sketch, "E165.trimOffspring", {"start": v(73.08, -26.18) * mm, "end": v(73.71, -25.82) * mm});
            skArc(sketch, "E166.trimOffspring", {"start": v(73.41, -25.3) * mm, "mid": v(71.44, -23.42) * mm, "end": v(68.82, -22.65) * mm});
            skArc(sketch, "E167.trimOffspring", {"start": v(72.78, -25.66) * mm, "mid": v(72.48, -25.25) * mm, "end": v(72.13, -24.86) * mm});
            skLineSegment(sketch, "E168.trimOffspring", {"start": v(73.08, -30.75) * mm, "end": v(73.71, -31.12) * mm});
            skLineSegment(sketch, "E169.trimOffspring", {"start": v(72.78, -31.27) * mm, "end": v(73.41, -31.64) * mm});
            skArc(sketch, "E170.trimOffspring", {"start": v(73.08, -30.75) * mm, "mid": v(73.3, -30.28) * mm, "end": v(73.45, -29.79) * mm});
            skArc(sketch, "E171.trimOffspring", {"start": v(73.71, -31.12) * mm, "mid": v(74.35, -28.47) * mm, "end": v(73.71, -25.82) * mm});
            skLineSegment(sketch, "E172", {"start": v(68.82, -34.3) * mm, "end": v(68.82, -33.56) * mm});
            skArc(sketch, "E173.trimOffspring", {"start": v(68.82, -33.56) * mm, "mid": v(69.34, -33.5) * mm, "end": v(69.84, -33.4) * mm});
            skArc(sketch, "E174.trimOffspring", {"start": v(68.82, -34.29) * mm, "mid": v(71.44, -33.51) * mm, "end": v(73.41, -31.64) * mm});
            skLineSegment(sketch, "E175.trimOffspring", {"start": v(71.66, -31.6) * mm, "end": v(72.13, -32.07) * mm});
            skArc(sketch, "E176.trimOffspring", {"start": v(72.81, -29.62) * mm, "mid": v(72.96, -28.47) * mm, "end": v(72.81, -27.32) * mm});
            skArc(sketch, "E177.trimOffspring", {"start": v(71.66, -25.33) * mm, "mid": v(70.74, -24.62) * mm, "end": v(69.67, -24.18) * mm});
            skLineSegment(sketch, "E178.trimOffspring", {"start": v(72.81, -27.32) * mm, "end": v(73.45, -27.15) * mm});
            skLineSegment(sketch, "E179.trimOffspring", {"start": v(71.66, -25.33) * mm, "end": v(72.13, -24.86) * mm});
            skLineSegment(sketch, "E180.trimOffspring", {"start": v(69.67, -24.18) * mm, "end": v(69.84, -23.54) * mm});
            skLineSegment(sketch, "E181", {"start": v(68.89, -26.6) * mm, "end": v(69.28, -24.6) * mm});
            skLineSegment(sketch, "E182", {"start": v(69.28, -24.6) * mm, "end": v(68.52, -24.6) * mm});
            skLineSegment(sketch, "E183", {"start": v(69.97, -27.21) * mm, "end": v(71.5, -25.88) * mm});
            skLineSegment(sketch, "E184", {"start": v(70.33, -27.85) * mm, "end": v(72.25, -27.19) * mm});
            skLineSegment(sketch, "E185", {"start": v(70.33, -29.1) * mm, "end": v(72.25, -29.75) * mm});
            skLineSegment(sketch, "E186", {"start": v(68.89, -30.35) * mm, "end": v(69.28, -32.33) * mm});
            skLineSegment(sketch, "E187", {"start": v(71.5, -25.88) * mm, "end": v(71.87, -26.54) * mm});
            skLineSegment(sketch, "E188", {"start": v(71.87, -26.54) * mm, "end": v(72.25, -27.19) * mm});
            skLineSegment(sketch, "E189", {"start": v(72.25, -29.75) * mm, "end": v(71.5, -31.05) * mm});
            skLineSegment(sketch, "E190", {"start": v(69.28, -32.33) * mm, "end": v(68.52, -32.33) * mm});
            skLineSegment(sketch, "E191.trimOffspring", {"start": v(69.67, -32.75) * mm, "end": v(69.84, -33.4) * mm});
            skLineSegment(sketch, "E192.trimOffspring", {"start": v(72.81, -29.62) * mm, "end": v(73.45, -29.79) * mm});
            skArc(sketch, "E193.trimOffspring", {"start": v(69.97, -27.21) * mm, "mid": v(69.48, -26.81) * mm, "end": v(68.89, -26.6) * mm});
            skArc(sketch, "E194.trimOffspring", {"start": v(68.89, -30.35) * mm, "mid": v(69.48, -30.12) * mm, "end": v(69.97, -29.72) * mm});
            skLineSegment(sketch, "E195", {"start": v(71.5, -31.05) * mm, "end": v(69.97, -29.72) * mm});
            skArc(sketch, "E196.trimOffspring", {"start": v(70.33, -29.1) * mm, "mid": v(70.44, -28.47) * mm, "end": v(70.33, -27.85) * mm});
            skLineSegment(sketch, "E197.MirrorCS", {"start": v(68.22, -22.64) * mm, "end": v(68.22, -23.38) * mm});
            skLineSegment(sketch, "E198.MirrorCS", {"start": v(68.22, -23.38) * mm, "end": v(68.22, -22.64) * mm});
            skLineSegment(sketch, "E199.MirrorCS", {"start": v(64.24, -27.32) * mm, "end": v(63.6, -27.15) * mm});
            skLineSegment(sketch, "E200.MirrorCS", {"start": v(65.18, -26.54) * mm, "end": v(64.8, -27.19) * mm});
            skLineSegment(sketch, "E201.MirrorCS", {"start": v(65.39, -25.33) * mm, "end": v(64.92, -24.86) * mm});
            skLineSegment(sketch, "E202.MirrorCS", {"start": v(63.96, -26.18) * mm, "end": v(63.34, -25.82) * mm});
            skLineSegment(sketch, "E203.MirrorCS", {"start": v(67.38, -24.18) * mm, "end": v(67.2, -23.54) * mm});
            skLineSegment(sketch, "E204.MirrorCS", {"start": v(65.55, -25.88) * mm, "end": v(65.18, -26.54) * mm});
            skLineSegment(sketch, "E205.MirrorCS", {"start": v(64.26, -31.27) * mm, "end": v(63.64, -31.64) * mm});
            skLineSegment(sketch, "E206.MirrorCS", {"start": v(64.26, -25.66) * mm, "end": v(63.64, -25.3) * mm});
            skLineSegment(sketch, "E207.MirrorCS", {"start": v(68.22, -34.3) * mm, "end": v(68.22, -33.56) * mm});
            skLineSegment(sketch, "E208.MirrorCS", {"start": v(65.39, -31.6) * mm, "end": v(64.92, -32.07) * mm});
            skLineSegment(sketch, "E209.MirrorCS", {"start": v(67.38, -32.75) * mm, "end": v(67.2, -33.4) * mm});
            skLineSegment(sketch, "E210.MirrorCS", {"start": v(64.24, -29.62) * mm, "end": v(63.6, -29.79) * mm});
            skLineSegment(sketch, "E211.MirrorCS", {"start": v(63.96, -30.75) * mm, "end": v(63.34, -31.12) * mm});
            skLineSegment(sketch, "E212.MirrorCS", {"start": v(67.77, -24.6) * mm, "end": v(68.52, -24.6) * mm});
            skLineSegment(sketch, "E213.MirrorCS", {"start": v(67.77, -32.33) * mm, "end": v(68.52, -32.33) * mm});
            skArc(sketch, "E214.MirrorCS", {"start": v(67.08, -27.21) * mm, "mid": v(67.57, -26.81) * mm, "end": v(68.16, -26.6) * mm});
            skArc(sketch, "E215.MirrorCS", {"start": v(63.34, -31.12) * mm, "mid": v(62.7, -28.47) * mm, "end": v(63.34, -25.82) * mm});
            skArc(sketch, "E216.MirrorCS", {"start": v(68.22, -33.56) * mm, "mid": v(67.7, -33.5) * mm, "end": v(67.2, -33.4) * mm});
            skArc(sketch, "E217.MirrorCS", {"start": v(64.92, -32.07) * mm, "mid": v(64.57, -31.7) * mm, "end": v(64.26, -31.27) * mm});
            skArc(sketch, "E218.MirrorCS", {"start": v(65.39, -25.33) * mm, "mid": v(66.3, -24.62) * mm, "end": v(67.38, -24.18) * mm});
            skArc(sketch, "E219.MirrorCS", {"start": v(63.96, -30.75) * mm, "mid": v(63.76, -30.28) * mm, "end": v(63.6, -29.79) * mm});
            skLineSegment(sketch, "E220.MirrorCS", {"start": v(68.16, -30.35) * mm, "end": v(67.77, -32.33) * mm});
            skArc(sketch, "E221.MirrorCS", {"start": v(68.16, -30.35) * mm, "mid": v(67.57, -30.12) * mm, "end": v(67.08, -29.72) * mm});
            skArc(sketch, "E222.MirrorCS", {"start": v(64.26, -25.66) * mm, "mid": v(64.57, -25.25) * mm, "end": v(64.92, -24.86) * mm});
            skArc(sketch, "E223.MirrorCS", {"start": v(64.24, -29.62) * mm, "mid": v(64.09, -28.47) * mm, "end": v(64.24, -27.32) * mm});
            skArc(sketch, "E224.MirrorCS", {"start": v(63.64, -25.3) * mm, "mid": v(65.61, -23.42) * mm, "end": v(68.22, -22.65) * mm});
            skLineSegment(sketch, "E225.MirrorCS", {"start": v(65.55, -31.05) * mm, "end": v(67.08, -29.72) * mm});
            skLineSegment(sketch, "E226.MirrorCS", {"start": v(66.72, -29.1) * mm, "end": v(64.8, -29.75) * mm});
            skArc(sketch, "E227.MirrorCS", {"start": v(67.2, -23.54) * mm, "mid": v(67.7, -23.43) * mm, "end": v(68.22, -23.38) * mm});
            skArc(sketch, "E228.MirrorCS", {"start": v(67.38, -32.75) * mm, "mid": v(66.3, -32.31) * mm, "end": v(65.39, -31.6) * mm});
            skLineSegment(sketch, "E229.MirrorCS", {"start": v(68.16, -26.6) * mm, "end": v(67.77, -24.6) * mm});
            skLineSegment(sketch, "E230.MirrorCS", {"start": v(64.8, -29.75) * mm, "end": v(65.55, -31.05) * mm});
            skArc(sketch, "E231.MirrorCS", {"start": v(63.6, -27.15) * mm, "mid": v(63.76, -26.66) * mm, "end": v(63.96, -26.18) * mm});
            skArc(sketch, "E232.MirrorCS", {"start": v(66.72, -29.1) * mm, "mid": v(66.61, -28.47) * mm, "end": v(66.72, -27.85) * mm});
            skArc(sketch, "E233.MirrorCS", {"start": v(68.22, -34.29) * mm, "mid": v(65.61, -33.51) * mm, "end": v(63.64, -31.64) * mm});
            skLineSegment(sketch, "E234.MirrorCS", {"start": v(66.72, -27.85) * mm, "end": v(64.8, -27.19) * mm});
            skLineSegment(sketch, "E235.MirrorCS", {"start": v(67.08, -27.21) * mm, "end": v(65.55, -25.88) * mm});
            skArc(sketch, "E236.MirrorCS", {"start": v(68.52, -34.97) * mm, "mid": v(62.02, -28.47) * mm, "end": v(68.52, -21.97) * mm});
            skArc(sketch, "E237", {"start": v(-34.38, 20.48) * mm, "mid": v(-34.76, 20.33) * mm, "end": v(-35.08, 20.08) * mm});
            skArc(sketch, "E238.0", {"start": v(-34.97, 22.19) * mm, "mid": v(-35.66, 21.9) * mm, "end": v(-36.27, 21.44) * mm});
            skArc(sketch, "E239.0", {"start": v(-34.3, 22.7) * mm, "mid": v(-34.7, 22.66) * mm, "end": v(-35.08, 22.57) * mm});
            skArc(sketch, "E240.0", {"start": v(-34.33, 23.25) * mm, "mid": v(-36.14, 22.71) * mm, "end": v(-37.51, 21.41) * mm});
            skArc(sketch, "E241.0", {"start": v(-29.61, 19.2) * mm, "mid": v(-34.11, 23.7) * mm, "end": v(-38.61, 19.2) * mm});
            skArc(sketch, "E242.0", {"start": v(-33.54, 21.9) * mm, "mid": v(-34.11, 21.96) * mm, "end": v(-34.69, 21.9) * mm});
            skLineSegment(sketch, "E243.trimOffspring", {"start": v(-34.3, 22.7) * mm, "end": v(-34.33, 23.25) * mm});
            skLineSegment(sketch, "E244.trimOffspring", {"start": v(-33.93, 22.7) * mm, "end": v(-33.9, 23.25) * mm});
            skArc(sketch, "E245.trimOffspring", {"start": v(-30.72, 21.41) * mm, "mid": v(-32.09, 22.71) * mm, "end": v(-33.9, 23.25) * mm});
            skArc(sketch, "E246.trimOffspring", {"start": v(-31.18, 21.11) * mm, "mid": v(-31.41, 21.43) * mm, "end": v(-31.68, 21.72) * mm});
            skArc(sketch, "E247.trimOffspring", {"start": v(-31.96, 21.44) * mm, "mid": v(-32.56, 21.9) * mm, "end": v(-33.26, 22.19) * mm});
            skLineSegment(sketch, "E248.trimOffspring", {"start": v(-31.18, 21.11) * mm, "end": v(-30.72, 21.41) * mm});
            skLineSegment(sketch, "E249.trimOffspring", {"start": v(-31, 20.8) * mm, "end": v(-30.5, 21.04) * mm});
            skLineSegment(sketch, "E250.trimOffspring", {"start": v(-33.26, 22.19) * mm, "end": v(-33.15, 22.57) * mm});
            skLineSegment(sketch, "E251.trimOffspring", {"start": v(-31.96, 21.44) * mm, "end": v(-31.68, 21.72) * mm});
            skLineSegment(sketch, "E252.trimOffspring", {"start": v(-34.97, 22.19) * mm, "end": v(-35.08, 22.57) * mm});
            skLineSegment(sketch, "E253.trimOffspring", {"start": v(-36.27, 21.44) * mm, "end": v(-36.54, 21.72) * mm});
            skArc(sketch, "E254.trimOffspring", {"start": v(-36.16, 21.05) * mm, "mid": v(-36.5, 20.58) * mm, "end": v(-36.73, 20.06) * mm});
            skLineSegment(sketch, "E255.trimOffspring", {"start": v(-31.1, 19.96) * mm, "end": v(-30.72, 20.05) * mm});
            skArc(sketch, "E256.trimOffspring", {"start": v(-31.5, 20.06) * mm, "mid": v(-31.73, 20.58) * mm, "end": v(-32.07, 21.05) * mm});
            skLineSegment(sketch, "E257.trimOffspring", {"start": v(-37.12, 19.96) * mm, "end": v(-37.5, 20.05) * mm});
            skArc(sketch, "E258.trimOffspring", {"start": v(-37.12, 19.96) * mm, "mid": v(-37.2, 19.58) * mm, "end": v(-37.21, 19.2) * mm});
            skArc(sketch, "E259.trimOffspring", {"start": v(-37.23, 20.8) * mm, "mid": v(-37.4, 20.43) * mm, "end": v(-37.5, 20.05) * mm});
            skArc(sketch, "E260.trimOffspring", {"start": v(-37.72, 21.04) * mm, "mid": v(-38.05, 20.15) * mm, "end": v(-38.16, 19.2) * mm});
            skLineSegment(sketch, "E261.trimOffspring", {"start": v(-37.05, 21.11) * mm, "end": v(-37.51, 21.41) * mm});
            skLineSegment(sketch, "E262.trimOffspring", {"start": v(-37.23, 20.8) * mm, "end": v(-37.72, 21.04) * mm});
            skArc(sketch, "E263.trimOffspring", {"start": v(-36.54, 21.72) * mm, "mid": v(-36.81, 21.43) * mm, "end": v(-37.05, 21.11) * mm});
            skArc(sketch, "E264.trimOffspring", {"start": v(-33.15, 22.57) * mm, "mid": v(-33.54, 22.66) * mm, "end": v(-33.93, 22.7) * mm});
            skArc(sketch, "E265.trimOffspring", {"start": v(-30.72, 20.05) * mm, "mid": v(-30.84, 20.43) * mm, "end": v(-31, 20.8) * mm});
            skLineSegment(sketch, "E266", {"start": v(-32.07, 21.05) * mm, "end": v(-33.15, 20.08) * mm});
            skLineSegment(sketch, "E267.trimOffspring", {"start": v(-33.84, 20.48) * mm, "end": v(-33.54, 21.9) * mm});
            skLineSegment(sketch, "E268.trimOffspring", {"start": v(-32.88, 19.6) * mm, "end": v(-31.5, 20.06) * mm});
            skLineSegment(sketch, "E269.trimOffspring", {"start": v(-35.35, 19.6) * mm, "end": v(-36.73, 20.06) * mm});
            skLineSegment(sketch, "E270.trimOffspring", {"start": v(-35.08, 20.08) * mm, "end": v(-36.16, 21.05) * mm});
            skLineSegment(sketch, "E271.trimOffspring", {"start": v(-34.38, 20.48) * mm, "end": v(-34.69, 21.9) * mm});
            skArc(sketch, "E272.trimOffspring", {"start": v(-35.35, 19.6) * mm, "mid": v(-35.4, 19.4) * mm, "end": v(-35.41, 19.2) * mm});
            skArc(sketch, "E273.trimOffspring", {"start": v(-33.15, 20.08) * mm, "mid": v(-33.46, 20.33) * mm, "end": v(-33.84, 20.48) * mm});
            skArc(sketch, "E274.trimOffspring", {"start": v(-31.01, 19.2) * mm, "mid": v(-31.04, 19.58) * mm, "end": v(-31.1, 19.96) * mm});
            skArc(sketch, "E275.trimOffspring", {"start": v(-30.06, 19.2) * mm, "mid": v(-30.18, 20.15) * mm, "end": v(-30.5, 21.04) * mm});
            skArc(sketch, "E276.trimOffspring", {"start": v(-32.81, 19.2) * mm, "mid": v(-32.83, 19.4) * mm, "end": v(-32.88, 19.6) * mm});
            skLineSegment(sketch, "E277.MirrorCS", {"start": v(-34.97, 16.23) * mm, "end": v(-35.08, 15.84) * mm});
            skLineSegment(sketch, "E278.MirrorCS", {"start": v(-37.05, 17.3) * mm, "end": v(-37.51, 17) * mm});
            skLineSegment(sketch, "E279.MirrorCS", {"start": v(-31.1, 18.46) * mm, "end": v(-30.72, 18.36) * mm});
            skLineSegment(sketch, "E280.MirrorCS", {"start": v(-33.26, 16.23) * mm, "end": v(-33.15, 15.84) * mm});
            skLineSegment(sketch, "E281.MirrorCS", {"start": v(-31.96, 16.98) * mm, "end": v(-31.68, 16.69) * mm});
            skLineSegment(sketch, "E282.MirrorCS", {"start": v(-37.12, 18.46) * mm, "end": v(-37.5, 18.36) * mm});
            skLineSegment(sketch, "E283.MirrorCS", {"start": v(-31.18, 17.3) * mm, "end": v(-30.72, 17) * mm});
            skLineSegment(sketch, "E284.MirrorCS", {"start": v(-36.27, 16.98) * mm, "end": v(-36.54, 16.69) * mm});
            skLineSegment(sketch, "E285.MirrorCS", {"start": v(-33.93, 15.71) * mm, "end": v(-33.9, 15.16) * mm});
            skArc(sketch, "E286.MirrorCS", {"start": v(-35.35, 18.8) * mm, "mid": v(-35.4, 19) * mm, "end": v(-35.41, 19.2) * mm});
            skArc(sketch, "E287.MirrorCS", {"start": v(-32.81, 19.2) * mm, "mid": v(-32.83, 19) * mm, "end": v(-32.88, 18.8) * mm});
            skLineSegment(sketch, "E288.MirrorCS", {"start": v(-32.07, 17.37) * mm, "end": v(-33.15, 18.34) * mm});
            skLineSegment(sketch, "E289.MirrorCS", {"start": v(-35.08, 18.34) * mm, "end": v(-36.16, 17.37) * mm});
            skArc(sketch, "E290.MirrorCS", {"start": v(-30.06, 19.2) * mm, "mid": v(-30.18, 18.26) * mm, "end": v(-30.5, 17.37) * mm});
            skArc(sketch, "E291.MirrorCS", {"start": v(-37.12, 18.46) * mm, "mid": v(-37.2, 18.83) * mm, "end": v(-37.21, 19.2) * mm});
            skArc(sketch, "E292.MirrorCS", {"start": v(-31.01, 19.2) * mm, "mid": v(-31.04, 18.83) * mm, "end": v(-31.1, 18.46) * mm});
            skLineSegment(sketch, "E293.MirrorCS", {"start": v(-34.3, 15.71) * mm, "end": v(-34.33, 15.16) * mm});
            skArc(sketch, "E294.MirrorCS", {"start": v(-33.15, 15.84) * mm, "mid": v(-33.54, 15.75) * mm, "end": v(-33.93, 15.71) * mm});
            skArc(sketch, "E295.MirrorCS", {"start": v(-31.96, 16.98) * mm, "mid": v(-32.56, 16.52) * mm, "end": v(-33.26, 16.23) * mm});
            skArc(sketch, "E296.MirrorCS", {"start": v(-30.72, 17) * mm, "mid": v(-32.09, 15.7) * mm, "end": v(-33.9, 15.16) * mm});
            skArc(sketch, "E297.MirrorCS", {"start": v(-34.97, 16.23) * mm, "mid": v(-35.66, 16.52) * mm, "end": v(-36.27, 16.98) * mm});
            skArc(sketch, "E298.MirrorCS", {"start": v(-34.38, 17.93) * mm, "mid": v(-34.76, 18.08) * mm, "end": v(-35.08, 18.34) * mm});
            skArc(sketch, "E299.MirrorCS", {"start": v(-36.54, 16.69) * mm, "mid": v(-36.81, 16.98) * mm, "end": v(-37.05, 17.3) * mm});
            skArc(sketch, "E300.MirrorCS", {"start": v(-34.33, 15.16) * mm, "mid": v(-36.14, 15.7) * mm, "end": v(-37.51, 17) * mm});
            skLineSegment(sketch, "E301.MirrorCS", {"start": v(-33.84, 17.93) * mm, "end": v(-33.54, 16.52) * mm});
            skArc(sketch, "E302.MirrorCS", {"start": v(-33.54, 16.52) * mm, "mid": v(-34.11, 16.46) * mm, "end": v(-34.69, 16.52) * mm});
            skArc(sketch, "E303.MirrorCS", {"start": v(-30.72, 18.36) * mm, "mid": v(-30.84, 17.98) * mm, "end": v(-31, 17.62) * mm});
            skLineSegment(sketch, "E304.MirrorCS", {"start": v(-37.23, 17.62) * mm, "end": v(-37.72, 17.37) * mm});
            skArc(sketch, "E305.MirrorCS", {"start": v(-31.18, 17.3) * mm, "mid": v(-31.41, 16.98) * mm, "end": v(-31.68, 16.69) * mm});
            skLineSegment(sketch, "E306.MirrorCS", {"start": v(-31, 17.62) * mm, "end": v(-30.5, 17.37) * mm});
            skLineSegment(sketch, "E307.MirrorCS", {"start": v(-32.88, 18.8) * mm, "end": v(-31.5, 18.36) * mm});
            skArc(sketch, "E308.MirrorCS", {"start": v(-37.72, 17.37) * mm, "mid": v(-38.05, 18.26) * mm, "end": v(-38.16, 19.2) * mm});
            skLineSegment(sketch, "E309.MirrorCS", {"start": v(-35.35, 18.8) * mm, "end": v(-36.73, 18.36) * mm});
            skLineSegment(sketch, "E310.MirrorCS", {"start": v(-34.38, 17.93) * mm, "end": v(-34.69, 16.52) * mm});
            skArc(sketch, "E311.MirrorCS", {"start": v(-34.3, 15.71) * mm, "mid": v(-34.7, 15.75) * mm, "end": v(-35.08, 15.84) * mm});
            skArc(sketch, "E312.MirrorCS", {"start": v(-33.15, 18.34) * mm, "mid": v(-33.46, 18.08) * mm, "end": v(-33.84, 17.93) * mm});
            skArc(sketch, "E313.MirrorCS", {"start": v(-36.16, 17.37) * mm, "mid": v(-36.5, 17.83) * mm, "end": v(-36.73, 18.36) * mm});
            skArc(sketch, "E314.MirrorCS", {"start": v(-29.61, 19.2) * mm, "mid": v(-34.11, 14.7) * mm, "end": v(-38.61, 19.2) * mm});
            skArc(sketch, "E315.MirrorCS", {"start": v(-37.23, 17.62) * mm, "mid": v(-37.4, 17.98) * mm, "end": v(-37.5, 18.36) * mm});
            skArc(sketch, "E316.MirrorCS", {"start": v(-31.5, 18.36) * mm, "mid": v(-31.73, 17.83) * mm, "end": v(-32.07, 17.37) * mm});
            skArc(sketch, "E317", {"start": v(35.62, 20.63) * mm, "mid": v(35.24, 20.49) * mm, "end": v(34.92, 20.23) * mm});
            skArc(sketch, "E318.0", {"start": v(35.03, 22.34) * mm, "mid": v(34.34, 22.05) * mm, "end": v(33.73, 21.6) * mm});
            skArc(sketch, "E319.0", {"start": v(35.7, 22.86) * mm, "mid": v(35.3, 22.81) * mm, "end": v(34.92, 22.73) * mm});
            skArc(sketch, "E320.0", {"start": v(35.67, 23.4) * mm, "mid": v(33.86, 22.87) * mm, "end": v(32.49, 21.57) * mm});
            skArc(sketch, "E321.0", {"start": v(40.39, 19.36) * mm, "mid": v(35.89, 23.86) * mm, "end": v(31.39, 19.36) * mm});
            skArc(sketch, "E322.0", {"start": v(36.46, 22.05) * mm, "mid": v(35.89, 22.11) * mm, "end": v(35.31, 22.05) * mm});
            skLineSegment(sketch, "E323.trimOffspring", {"start": v(35.7, 22.86) * mm, "end": v(35.67, 23.4) * mm});
            skLineSegment(sketch, "E324.trimOffspring", {"start": v(36.07, 22.86) * mm, "end": v(36.1, 23.4) * mm});
            skArc(sketch, "E325.trimOffspring", {"start": v(39.28, 21.57) * mm, "mid": v(37.91, 22.87) * mm, "end": v(36.1, 23.4) * mm});
            skArc(sketch, "E326.trimOffspring", {"start": v(38.82, 21.27) * mm, "mid": v(38.59, 21.59) * mm, "end": v(38.32, 21.88) * mm});
            skArc(sketch, "E327.trimOffspring", {"start": v(38.04, 21.6) * mm, "mid": v(37.44, 22.05) * mm, "end": v(36.74, 22.34) * mm});
            skLineSegment(sketch, "E328.trimOffspring", {"start": v(38.82, 21.27) * mm, "end": v(39.28, 21.57) * mm});
            skLineSegment(sketch, "E329.trimOffspring", {"start": v(39, 20.95) * mm, "end": v(39.5, 21.2) * mm});
            skLineSegment(sketch, "E330.trimOffspring", {"start": v(36.74, 22.34) * mm, "end": v(36.85, 22.73) * mm});
            skLineSegment(sketch, "E331.trimOffspring", {"start": v(38.04, 21.6) * mm, "end": v(38.32, 21.88) * mm});
            skLineSegment(sketch, "E332.trimOffspring", {"start": v(35.03, 22.34) * mm, "end": v(34.92, 22.73) * mm});
            skLineSegment(sketch, "E333.trimOffspring", {"start": v(33.73, 21.6) * mm, "end": v(33.46, 21.88) * mm});
            skArc(sketch, "E334.trimOffspring", {"start": v(33.84, 21.2) * mm, "mid": v(33.5, 20.74) * mm, "end": v(33.27, 20.21) * mm});
            skLineSegment(sketch, "E335.trimOffspring", {"start": v(38.9, 20.11) * mm, "end": v(39.28, 20.2) * mm});
            skArc(sketch, "E336.trimOffspring", {"start": v(38.5, 20.21) * mm, "mid": v(38.27, 20.74) * mm, "end": v(37.93, 21.2) * mm});
            skLineSegment(sketch, "E337.trimOffspring", {"start": v(32.88, 20.11) * mm, "end": v(32.5, 20.2) * mm});
            skArc(sketch, "E338.trimOffspring", {"start": v(32.88, 20.11) * mm, "mid": v(32.8, 19.74) * mm, "end": v(32.79, 19.36) * mm});
            skArc(sketch, "E339.trimOffspring", {"start": v(32.77, 20.95) * mm, "mid": v(32.6, 20.59) * mm, "end": v(32.5, 20.2) * mm});
            skArc(sketch, "E340.trimOffspring", {"start": v(32.28, 21.2) * mm, "mid": v(31.95, 20.3) * mm, "end": v(31.84, 19.36) * mm});
            skLineSegment(sketch, "E341.trimOffspring", {"start": v(32.95, 21.27) * mm, "end": v(32.49, 21.57) * mm});
            skLineSegment(sketch, "E342.trimOffspring", {"start": v(32.77, 20.95) * mm, "end": v(32.28, 21.2) * mm});
            skArc(sketch, "E343.trimOffspring", {"start": v(33.46, 21.88) * mm, "mid": v(33.19, 21.59) * mm, "end": v(32.95, 21.27) * mm});
            skArc(sketch, "E344.trimOffspring", {"start": v(36.85, 22.73) * mm, "mid": v(36.46, 22.81) * mm, "end": v(36.07, 22.86) * mm});
            skArc(sketch, "E345.trimOffspring", {"start": v(39.28, 20.2) * mm, "mid": v(39.16, 20.59) * mm, "end": v(39, 20.95) * mm});
            skLineSegment(sketch, "E346", {"start": v(37.93, 21.2) * mm, "end": v(36.85, 20.23) * mm});
            skLineSegment(sketch, "E347.trimOffspring", {"start": v(36.16, 20.63) * mm, "end": v(36.46, 22.05) * mm});
            skLineSegment(sketch, "E348.trimOffspring", {"start": v(37.12, 19.76) * mm, "end": v(38.5, 20.21) * mm});
            skLineSegment(sketch, "E349.trimOffspring", {"start": v(34.65, 19.76) * mm, "end": v(33.27, 20.21) * mm});
            skLineSegment(sketch, "E350.trimOffspring", {"start": v(34.92, 20.23) * mm, "end": v(33.84, 21.2) * mm});
            skLineSegment(sketch, "E351.trimOffspring", {"start": v(35.62, 20.63) * mm, "end": v(35.31, 22.05) * mm});
            skArc(sketch, "E352.trimOffspring", {"start": v(34.65, 19.76) * mm, "mid": v(34.6, 19.57) * mm, "end": v(34.59, 19.36) * mm});
            skArc(sketch, "E353.trimOffspring", {"start": v(36.85, 20.23) * mm, "mid": v(36.54, 20.49) * mm, "end": v(36.16, 20.63) * mm});
            skArc(sketch, "E354.trimOffspring", {"start": v(38.99, 19.36) * mm, "mid": v(38.96, 19.74) * mm, "end": v(38.9, 20.11) * mm});
            skArc(sketch, "E355.trimOffspring", {"start": v(39.94, 19.36) * mm, "mid": v(39.82, 20.3) * mm, "end": v(39.5, 21.2) * mm});
            skArc(sketch, "E356.trimOffspring", {"start": v(37.19, 19.36) * mm, "mid": v(37.17, 19.57) * mm, "end": v(37.12, 19.76) * mm});
            skLineSegment(sketch, "E357.MirrorCS", {"start": v(35.03, 16.38) * mm, "end": v(34.92, 16) * mm});
            skLineSegment(sketch, "E358.MirrorCS", {"start": v(32.95, 17.46) * mm, "end": v(32.49, 17.16) * mm});
            skLineSegment(sketch, "E359.MirrorCS", {"start": v(38.9, 18.61) * mm, "end": v(39.28, 18.52) * mm});
            skLineSegment(sketch, "E360.MirrorCS", {"start": v(36.74, 16.38) * mm, "end": v(36.85, 16) * mm});
            skLineSegment(sketch, "E361.MirrorCS", {"start": v(38.04, 17.13) * mm, "end": v(38.32, 16.85) * mm});
            skLineSegment(sketch, "E362.MirrorCS", {"start": v(32.88, 18.61) * mm, "end": v(32.5, 18.52) * mm});
            skLineSegment(sketch, "E363.MirrorCS", {"start": v(38.82, 17.46) * mm, "end": v(39.28, 17.16) * mm});
            skLineSegment(sketch, "E364.MirrorCS", {"start": v(33.73, 17.13) * mm, "end": v(33.46, 16.85) * mm});
            skLineSegment(sketch, "E365.MirrorCS", {"start": v(36.07, 15.87) * mm, "end": v(36.1, 15.32) * mm});
            skArc(sketch, "E366.MirrorCS", {"start": v(34.65, 18.96) * mm, "mid": v(34.6, 19.16) * mm, "end": v(34.59, 19.36) * mm});
            skArc(sketch, "E367.MirrorCS", {"start": v(37.19, 19.36) * mm, "mid": v(37.17, 19.16) * mm, "end": v(37.12, 18.96) * mm});
            skLineSegment(sketch, "E368.MirrorCS", {"start": v(37.93, 17.52) * mm, "end": v(36.85, 18.5) * mm});
            skLineSegment(sketch, "E369.MirrorCS", {"start": v(34.92, 18.5) * mm, "end": v(33.84, 17.52) * mm});
            skArc(sketch, "E370.MirrorCS", {"start": v(39.94, 19.36) * mm, "mid": v(39.82, 18.42) * mm, "end": v(39.5, 17.52) * mm});
            skArc(sketch, "E371.MirrorCS", {"start": v(32.88, 18.61) * mm, "mid": v(32.8, 18.99) * mm, "end": v(32.79, 19.36) * mm});
            skArc(sketch, "E372.MirrorCS", {"start": v(38.99, 19.36) * mm, "mid": v(38.96, 18.99) * mm, "end": v(38.9, 18.61) * mm});
            skLineSegment(sketch, "E373.MirrorCS", {"start": v(35.7, 15.87) * mm, "end": v(35.67, 15.32) * mm});
            skArc(sketch, "E374.MirrorCS", {"start": v(36.85, 16) * mm, "mid": v(36.46, 15.91) * mm, "end": v(36.07, 15.87) * mm});
            skArc(sketch, "E375.MirrorCS", {"start": v(38.04, 17.13) * mm, "mid": v(37.44, 16.68) * mm, "end": v(36.74, 16.38) * mm});
            skArc(sketch, "E376.MirrorCS", {"start": v(39.28, 17.16) * mm, "mid": v(37.91, 15.86) * mm, "end": v(36.1, 15.32) * mm});
            skArc(sketch, "E377.MirrorCS", {"start": v(35.03, 16.38) * mm, "mid": v(34.34, 16.68) * mm, "end": v(33.73, 17.13) * mm});
            skArc(sketch, "E378.MirrorCS", {"start": v(35.62, 18.1) * mm, "mid": v(35.24, 18.24) * mm, "end": v(34.92, 18.5) * mm});
            skArc(sketch, "E379.MirrorCS", {"start": v(33.46, 16.85) * mm, "mid": v(33.19, 17.14) * mm, "end": v(32.95, 17.46) * mm});
            skArc(sketch, "E380.MirrorCS", {"start": v(35.67, 15.32) * mm, "mid": v(33.86, 15.86) * mm, "end": v(32.49, 17.16) * mm});
            skLineSegment(sketch, "E381.MirrorCS", {"start": v(36.16, 18.1) * mm, "end": v(36.46, 16.67) * mm});
            skArc(sketch, "E382.MirrorCS", {"start": v(36.46, 16.67) * mm, "mid": v(35.89, 16.61) * mm, "end": v(35.31, 16.67) * mm});
            skArc(sketch, "E383.MirrorCS", {"start": v(39.28, 18.52) * mm, "mid": v(39.16, 18.14) * mm, "end": v(39, 17.77) * mm});
            skLineSegment(sketch, "E384.MirrorCS", {"start": v(32.77, 17.77) * mm, "end": v(32.28, 17.52) * mm});
            skArc(sketch, "E385.MirrorCS", {"start": v(38.82, 17.46) * mm, "mid": v(38.59, 17.14) * mm, "end": v(38.32, 16.85) * mm});
            skLineSegment(sketch, "E386.MirrorCS", {"start": v(39, 17.77) * mm, "end": v(39.5, 17.52) * mm});
            skLineSegment(sketch, "E387.MirrorCS", {"start": v(37.12, 18.96) * mm, "end": v(38.5, 18.51) * mm});
            skArc(sketch, "E388.MirrorCS", {"start": v(32.28, 17.52) * mm, "mid": v(31.95, 18.42) * mm, "end": v(31.84, 19.36) * mm});
            skLineSegment(sketch, "E389.MirrorCS", {"start": v(34.65, 18.96) * mm, "end": v(33.27, 18.51) * mm});
            skLineSegment(sketch, "E390.MirrorCS", {"start": v(35.62, 18.1) * mm, "end": v(35.31, 16.67) * mm});
            skArc(sketch, "E391.MirrorCS", {"start": v(35.7, 15.87) * mm, "mid": v(35.3, 15.91) * mm, "end": v(34.92, 16) * mm});
            skArc(sketch, "E392.MirrorCS", {"start": v(36.85, 18.5) * mm, "mid": v(36.54, 18.24) * mm, "end": v(36.16, 18.1) * mm});
            skArc(sketch, "E393.MirrorCS", {"start": v(33.84, 17.52) * mm, "mid": v(33.5, 17.99) * mm, "end": v(33.27, 18.51) * mm});
            skArc(sketch, "E394.MirrorCS", {"start": v(40.39, 19.36) * mm, "mid": v(35.89, 14.86) * mm, "end": v(31.39, 19.36) * mm});
            skArc(sketch, "E395.MirrorCS", {"start": v(32.77, 17.77) * mm, "mid": v(32.6, 18.14) * mm, "end": v(32.5, 18.52) * mm});
            skArc(sketch, "E396.MirrorCS", {"start": v(38.5, 18.51) * mm, "mid": v(38.27, 17.99) * mm, "end": v(37.93, 17.52) * mm});
            skPoint(sketch, "E397.0", {"position": v(35.89, 14.47) * mm});
            skPoint(sketch, "E398.0", {"position": v(35.89, 24.26) * mm});
            skLineSegment(sketch, "E399", {"start": v(35.89, 14.47) * mm, "end": v(35.89, 24.26) * mm, "construction": true});
            skText(sketch, "E400", { "text": "TIE", "fontName": "NotoSans-Bold.ttf"});
            skPoint(sketch, "E401.0", {"position": v(-10.64, 19.21) * mm});
            skPoint(sketch, "E401.1", {"position": v(12.41, 19.21) * mm});
            skPoint(sketch, "E401.2", {"position": v(0.89, 24.26) * mm});
            skPoint(sketch, "E401.3", {"position": v(-4.74, 16.23) * mm});
            skLineSegment(sketch, "E402", {"start": v(-10.64, 20.21) * mm, "end": v(12.41, 20.21) * mm, "construction": true});
            skLineSegment(sketch, "E403", {"start": v(0.89, 24.26) * mm, "end": v(0.89, 16.23) * mm, "construction": true});
            skText(sketch, "E404", { "text": "Fighter", "fontName": "NotoSans-Bold.ttf"});
            skLineSegment(sketch, "E405.0", {"start": v(-47.4, -25.17) * mm, "end": v(-47.4, -37.17) * mm});
            skLineSegment(sketch, "E405.1", {"start": v(45.64, -37.17) * mm, "end": v(45.64, -25.17) * mm});
            skPoint(sketch, "E405.2", {"position": v(-0.89, -31.17) * mm});
            skPoint(sketch, "E405.3", {"position": v(-35.89, -31.17) * mm});
            skPoint(sketch, "E405.4", {"position": v(34.11, -31.17) * mm});
            skLineSegment(sketch, "E406", {"start": v(-47.41, -34.29) * mm, "end": v(45.64, -34.29) * mm, "construction": true});
            skPoint(sketch, "E407.0", {"position": v(34.11, -37.17) * mm});
            skPoint(sketch, "E407.1", {"position": v(-35.89, -37.17) * mm});
            skPoint(sketch, "E407.2", {"position": v(-0.89, -37.17) * mm});
            skLineSegment(sketch, "E408", {"start": v(-35.89, -31.17) * mm, "end": v(-35.89, -37.17) * mm, "construction": true});
            skLineSegment(sketch, "E409", {"start": v(-0.89, -31.17) * mm, "end": v(-0.89, -37.17) * mm, "construction": true});
            skLineSegment(sketch, "E410", {"start": v(34.11, -31.17) * mm, "end": v(34.11, -37.17) * mm, "construction": true});
            skText(sketch, "E411", { "text": "F/O", "fontName": "NotoSans-Bold.ttf"});
            skText(sketch, "E412", { "text": "S/F", "fontName": "NotoSans-Bold.ttf"});
            const initialGuessF18  = {"E400": [-0.00604, 0.01696, 1, 0, 0.0065], "E404": [-0.01259, -0.03658, 1, 0, 0.0046], "E411": [-0.04152, -0.03658, 1, 0, 0.0046], "E412": [0.02924, -0.03658, 1, 0, 0.0046]};
            skSetInitialGuess(sketch, initialGuessF18);
            skSolve(sketch);
        }
        {
            var Q0;
            Q0=makeQuery(id+"F18.imprint","IMPRINT",FACE,{"disambiguationData":[TD([[makeQuery(id+"F18.imprint","IMPRINT",EDGE,{"derivedFrom":sQuery(id+"F18.wireOp",EDGE,"E400.sketch_text.stroke-0")}),-1.0]])]});
            var Q1;
            Q1=makeQuery(id+"F18.imprint","IMPRINT",FACE,{"disambiguationData":[TD([[makeQuery(id+"F18.imprint","IMPRINT",EDGE,{"derivedFrom":sQuery(id+"F18.wireOp",EDGE,"E400.sketch_text.stroke-8")}),-1.0]])]});
            var Q2;
            Q2=makeQuery(id+"F18.imprint","IMPRINT",FACE,{"disambiguationData":[TD([[makeQuery(id+"F18.imprint","IMPRINT",EDGE,{"derivedFrom":sQuery(id+"F18.wireOp",EDGE,"E400.sketch_text.stroke-20")}),-1.0]])]});
            var Q3;
            Q3=makeQuery(id+"F18.imprint","IMPRINT",FACE,{"disambiguationData":[TD([[makeQuery(id+"F18.imprint","IMPRINT",EDGE,{"derivedFrom":sQuery(id+"F18.wireOp",EDGE,"E404.sketch_text.stroke-0")}),-1.0]])]});
            var Q4;
            Q4=makeQuery(id+"F18.imprint","IMPRINT",FACE,{"disambiguationData":[TD([[makeQuery(id+"F18.imprint","IMPRINT",EDGE,{"derivedFrom":sQuery(id+"F18.wireOp",EDGE,"E404.sketch_text.stroke-10")}),-1.0]])]});
            var Q5;
            Q5=makeQuery(id+"F18.imprint","IMPRINT",FACE,{"disambiguationData":[TD([[makeQuery(id+"F18.imprint","IMPRINT",EDGE,{"derivedFrom":sQuery(id+"F18.wireOp",EDGE,"E404.sketch_text.stroke-15")}),-1.0]])]});
            var Q6;
            Q6=makeQuery(id+"F18.imprint","IMPRINT",FACE,{"disambiguationData":[TD([[makeQuery(id+"F18.imprint","IMPRINT",EDGE,{"derivedFrom":sQuery(id+"F18.wireOp",EDGE,"E404.sketch_text.stroke-46")}),-1.0]])]});
            var Q7;
            Q7=makeQuery(id+"F18.imprint","IMPRINT",FACE,{"disambiguationData":[TD([[makeQuery(id+"F18.imprint","IMPRINT",EDGE,{"derivedFrom":sQuery(id+"F18.wireOp",EDGE,"E404.sketch_text.stroke-63")}),-1.0]])]});
            var Q8;
            Q8=makeQuery(id+"F18.imprint","IMPRINT",FACE,{"disambiguationData":[TD([[makeQuery(id+"F18.imprint","IMPRINT",EDGE,{"derivedFrom":sQuery(id+"F18.wireOp",EDGE,"E404.sketch_text.stroke-101")}),-1.0]])]});
            var Q9;
            Q9=makeQuery(id+"F18.imprint","IMPRINT",FACE,{"disambiguationData":[TD([[makeQuery(id+"F18.imprint","IMPRINT",EDGE,{"derivedFrom":sQuery(id+"F18.wireOp",EDGE,"E411.sketch_text.stroke-0")}),-1.0]])]});
            var Q10;
            Q10=makeQuery(id+"F18.imprint","IMPRINT",FACE,{"disambiguationData":[TD([[makeQuery(id+"F18.imprint","IMPRINT",EDGE,{"derivedFrom":sQuery(id+"F18.wireOp",EDGE,"E411.sketch_text.stroke-10")}),-1.0]])]});
            var Q11;
            Q11=makeQuery(id+"F18.imprint","IMPRINT",FACE,{"disambiguationData":[TD([[makeQuery(id+"F18.imprint","IMPRINT",EDGE,{"derivedFrom":sQuery(id+"F18.wireOp",EDGE,"E412.sketch_text.stroke-0")}),-1.0]])]});
            var Q12;
            Q12=makeQuery(id+"F18.imprint","IMPRINT",FACE,{"disambiguationData":[TD([[makeQuery(id+"F18.imprint","IMPRINT",EDGE,{"derivedFrom":sQuery(id+"F18.wireOp",EDGE,"E412.sketch_text.stroke-28")}),-1.0]])]});
            var Q13;
            Q13=makeQuery(id+"F18.imprint","IMPRINT",FACE,{"disambiguationData":[TD([[makeQuery(id+"F18.imprint","IMPRINT",EDGE,{"derivedFrom":sQuery(id+"F18.wireOp",EDGE,"E412.sketch_text.stroke-32")}),-1.0]])]});
            var Q14;
            Q14=makeQuery(id+"F18.imprint","IMPRINT",FACE,{"disambiguationData":[TD([[makeQuery(id+"F18.imprint","IMPRINT",EDGE,{"derivedFrom":sQuery(id+"F18.wireOp",EDGE,"E404.sketch_text.stroke-19")}),-1.0]])]});
            var Q15;
            Q15=makeQuery(id+"F18.imprint","IMPRINT",FACE,{"disambiguationData":[TD([[makeQuery(id+"F18.imprint","IMPRINT",EDGE,{"derivedFrom":sQuery(id+"F18.wireOp",EDGE,"E404.sketch_text.stroke-81")}),-1.0]])]});
            var Q16;
            Q16=makeQuery(id+"F18.imprint","IMPRINT",FACE,{"disambiguationData":[TD([[makeQuery(id+"F18.imprint","IMPRINT",EDGE,{"derivedFrom":sQuery(id+"F18.wireOp",EDGE,"E411.sketch_text.stroke-14")}),-1.0]])]});
            var Q17;
            Q17=makeQuery(id+"F18.imprint","IMPRINT",FACE,{"disambiguationData":[TD([[makeQuery(id+"F18.imprint","IMPRINT",EDGE,{"derivedFrom":sQuery(id+"F18.wireOp",EDGE,"E317")}),-1.0]])]});
            var Q18;
            Q18=makeQuery(id+"F18.imprint","IMPRINT",FACE,{"disambiguationData":[TD([[makeQuery(id+"F18.imprint","IMPRINT",EDGE,{"derivedFrom":sQuery(id+"F18.wireOp",EDGE,"E237")}),-1.0]])]});
            extrude(context, id + "F19", {"entities" : qUnion([Q0, Q1, Q2, Q3, Q4, Q5, Q6, Q7, Q8, Q9, Q10, Q11, Q12, Q13, Q14, Q15, Q16, Q17, Q18]), "operationType" : NewBodyOperationType.ADD, "depth" : 1 * mm, "offsetDistance" : 25 * mm});
        }
    });
